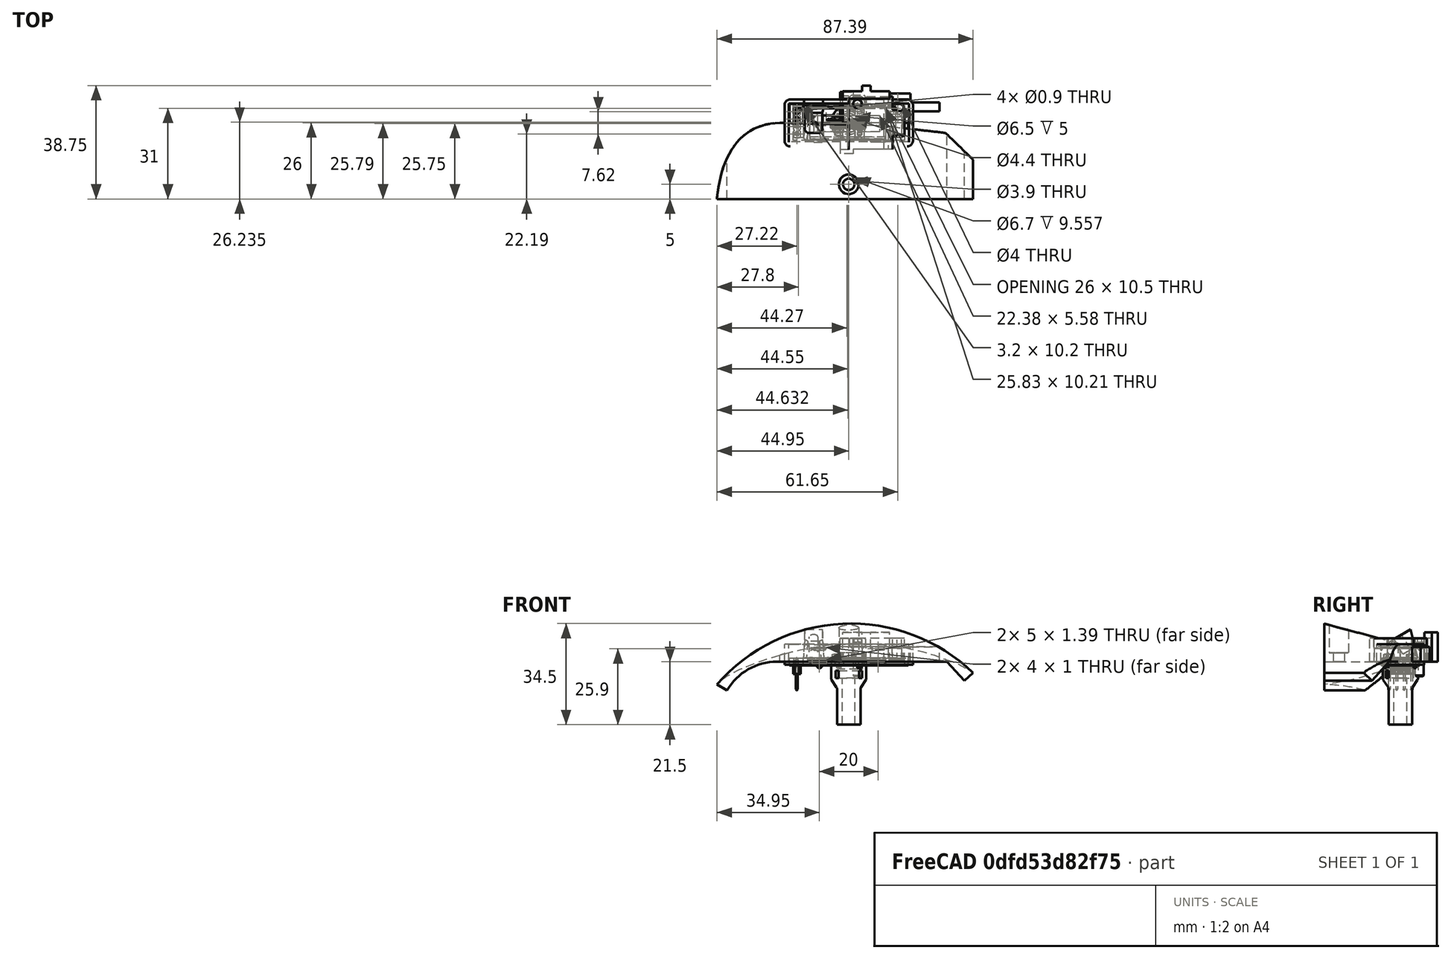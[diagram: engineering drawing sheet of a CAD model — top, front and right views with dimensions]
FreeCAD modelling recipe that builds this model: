
FCSTD DOCUMENT  (FreeCAD 1.0RUnknown)
Label: replicazeron
License: All rights reserved
LicenseURL: http://en.wikipedia.org/wiki/All_rights_reserved
objects: App::FeaturePython×45, Sketcher::SketchObject×26, Part::FeaturePython×17, PartDesign::CoordinateSystem×12, PartDesign::Pocket×10, PartDesign::Pad×8, App::Link×7, PartDesign::Body×7, App::DocumentObjectGroup×3, App::Part×3, PartDesign::Chamfer×3, PartDesign::Plane×2, PartDesign::Fillet×2, PartDesign::AdditiveLoft×2, PartDesign::Mirrored×2, Mesh::Feature×1, PartDesign::Revolution×1, PartDesign::SubtractiveLoft×1, PartDesign::PolarPattern×1, PartDesign::Hole×1
note: 180 computed .brp shape members not serialized (recipe doc carries the construction recipe); baked Part::Feature solids carry a one-line shape summary decoded from their .brp

FEATURE [PartDesign::CoordinateSystem] LCS_Origin
  AttacherType = Attacher::AttachEngine3D
  AttachmentSupport = -> [X_Axis]
  MapMode = 2
FEATURE [App::DocumentObjectGroup] Constraints
FEATURE [App::FeaturePython] Variables  # WARN: FeaturePython — macro-defined, semantics opaque (R4)
  Type = App::PropertyContainer
FEATURE [App::DocumentObjectGroup] Configurations
FEATURE [PartDesign::CoordinateSystem] LCS_0
  AttacherType = Attacher::AttachEngine3D
  AttachmentSupport = -> [X_Axis001]
  MapMode = 2
FEATURE [Sketcher::SketchObject] Sketch
  ArcFitTolerance = 0
  AttachmentSupport = -> [XY_Plane001]
  FullyConstrained = true
  MakeInternals = false
  MapMode = 5
  sketch-geometry (13):
    g0: LineSegment StartX=1.5 StartY=9 StartZ=0 EndX=15 EndY=9 EndZ=0
    g1: LineSegment StartX=15 StartY=-9 StartZ=0 EndX=1.5 EndY=-9 EndZ=0
    g2: LineSegment StartX=15 StartY=9 StartZ=0 EndX=15 EndY=4.5 EndZ=0
    g3: LineSegment StartX=15 StartY=4.5 StartZ=0 EndX=19 EndY=4.5 EndZ=0
    g4: LineSegment StartX=19 StartY=4.5 StartZ=0 EndX=19 EndY=-4.5 EndZ=0
    g5: LineSegment StartX=19 StartY=-4.5 StartZ=0 EndX=15 EndY=-4.5 EndZ=0
    g6: LineSegment StartX=15 StartY=-4.5 StartZ=0 EndX=15 EndY=-9 EndZ=0
    g7: LineSegment StartX=-3 StartY=10.5 StartZ=0 EndX=-3 EndY=-10.5 EndZ=0
    g8: LineSegment StartX=-3 StartY=10.5 StartZ=0 EndX=1.5 EndY=10.5 EndZ=0
    g9: LineSegment StartX=1.5 StartY=10.5 StartZ=0 EndX=1.5 EndY=9 EndZ=0
    g10: LineSegment StartX=1.5 StartY=-9 StartZ=0 EndX=1.5 EndY=-10.5 EndZ=0
    g11: LineSegment StartX=1.5 StartY=-10.5 StartZ=0 EndX=-3 EndY=-10.5 EndZ=0
    g12: LineSegment [constr] StartX=1.5 StartY=9 StartZ=0 EndX=1.5 EndY=-9 EndZ=0
  constraints (36):
    c: Horizontal(g0)
    c: Horizontal(g1)
    c: Symmetric(g0,g1,g-1)
    c: Coincident(g0,g2)
    c: Vertical(g2)
    c: Coincident(g2,g3)
    c: Horizontal(g3)
    c: Coincident(g3,g4)
    c: Coincident(g4,g5)
    c: Horizontal(g5)
    c: Coincident(g5,g6)
    c: Coincident(g6,g1)
    c: Vertical(g6)
    c: Symmetric(g4,g3,g-1)
    c: DistanceX(g3,g3) = 4
    c: DistanceY(g4,g4) = 9
    c: DistanceY(g1,g0) = 18
    c: Vertical(g7)
    c: Coincident(g7,g8)
    c: Horizontal(g8)
    c: Coincident(g8,g9)
    c: Coincident(g9,g0)
    c: Coincident(g1,g10)
    c: Coincident(g10,g11)
    c: Coincident(g11,g7)
    c: Horizontal(g11)
    c: Equal(g9,g10)
    c: DistanceY(g10,g10) = 1.5
    c: Vertical(g10)
    c: DistanceX(g3) = 19
    c: Vertical(g9)
    c: Coincident(g12,g0)
    c: Coincident(g12,g1)
    c: Vertical(g12)
    c: DistanceX(g7) = -3
    c: DistanceX(g0) = 1.5
FEATURE [PartDesign::Pad] Pad
  Direction = (0,0,1)
  Length = 8
  Length2 = 10
  Profile = -> Sketch
  ReferenceAxis = -> Sketch [N_Axis]
  Suppressed = false
  Type = 0
FEATURE [Sketcher::SketchObject] Sketch001
  ArcFitTolerance = 0
  AttachmentSupport = -> [XZ_Plane001]
  FullyConstrained = true
  MakeInternals = false
  MapMode = 5
  Placement = pos=(0,0,0) rot=(1,0,0;1.5708rad)
  sketch-geometry (4):
    g0: LineSegment StartX=-10 StartY=15 StartZ=0 EndX=0 EndY=15 EndZ=0
    g1: LineSegment StartX=0 StartY=15 StartZ=0 EndX=0 EndY=5 EndZ=0
    g2: LineSegment StartX=0 StartY=5 StartZ=0 EndX=-10 EndY=5 EndZ=0
    g3: LineSegment StartX=-10 StartY=5 StartZ=0 EndX=-10 EndY=15 EndZ=0
  constraints (12):
    c: Coincident(g0,g1)
    c: Coincident(g1,g2)
    c: Coincident(g2,g3)
    c: Coincident(g3,g0)
    c: Horizontal(g0)
    c: Horizontal(g2)
    c: Vertical(g1)
    c: Vertical(g3)
    c: PointOnObject(g0,g-2)
    c: DistanceY(g2) = 5
    c: Equal(g3,g2)
    c: DistanceX(g0,g0) = 10
FEATURE [PartDesign::Pocket] Pocket
  BaseFeature = -> Pad
  Direction = (0,1,-2e-16)
  Length = 18.2
  Length2 = 5
  Midplane = true
  Profile = -> Sketch001
  ReferenceAxis = -> Sketch001 [N_Axis]
  Suppressed = false
  Type = 0
FEATURE [Mesh::Feature] Thumb_spacer  label="Thumb spacer"
FEATURE [PartDesign::CoordinateSystem] LCS_0002
  AttacherType = Attacher::AttachEngine3D
  AttachmentSupport = -> [X_Axis003]
  MapMode = 2
FEATURE [Sketcher::SketchObject] Sketch005
  ArcFitTolerance = 0
  AttachmentSupport = -> [XY_Plane003]
  FullyConstrained = true
  MakeInternals = false
  MapMode = 5
  sketch-geometry (6):
    g0: LineSegment StartX=0 StartY=9.5 StartZ=0 EndX=6 EndY=9.5 EndZ=0
    g1: LineSegment StartX=6 StartY=9.5 StartZ=0 EndX=6 EndY=0 EndZ=0
    g2: LineSegment StartX=6 StartY=0 StartZ=0 EndX=0 EndY=0 EndZ=0
    g3: LineSegment StartX=0 StartY=0 StartZ=0 EndX=0 EndY=9.5 EndZ=0
    g4: Circle CenterX=3 CenterY=6.5 CenterZ=0 NormalX=0 NormalY=0 NormalZ=1 AngleXU=0 Radius=1.7
    g5: LineSegment [constr] StartX=0 StartY=6.5 StartZ=0 EndX=6 EndY=6.5 EndZ=0
  constraints (17):
    c: Coincident(g0,g1)
    c: Coincident(g1,g2)
    c: Coincident(g2,g3)
    c: Coincident(g3,g0)
    c: Horizontal(g0)
    c: Horizontal(g2)
    c: Vertical(g1)
    c: Vertical(g3)
    c: DistanceX(g0,g0) = 6
    c: DistanceY(g3,g3) = 9.5
    c: Coincident(g2,g-1)
    c: PointOnObject(g5,g3)
    c: PointOnObject(g5,g1)
    c: Horizontal(g5)
    c: Symmetric(g5,g5,g4)
    c: Diameter(g4) = 3.4
    c: DistanceY(g4) = 6.5
FEATURE [PartDesign::Pad] Pad002
  Direction = (0,0,1)
  Length = 5
  Length2 = 10
  Profile = -> Sketch005
  ReferenceAxis = -> Sketch005 [N_Axis]
  Suppressed = false
  Type = 0
FEATURE [PartDesign::CoordinateSystem] LCS_0003
  AttacherType = Attacher::AttachEngine3D
  AttachmentOffset = pos=(18.69,24.5,43) rot=(1,0,0;0.698132rad)
  AttachmentSupport = -> [X_Axis004]
  MapMode = 2
  Placement = pos=(18.69,24.5,43) rot=(1,0,0;0.698132rad)
FEATURE [App::Part] p_thumb_spacer
  Group = -> [LCS_0003,Thumb_spacer]
  Origin = -> Origin004
FEATURE [App::Link] thumb_spacer
  AssemblyType = Part::Link
  AttachedBy = #LCS_0003
  AttachedTo = Parent Assembly#LCS_Origin
  LinkPlacement = pos=(-18.69,-46.408,-17.1916) rot=(-1,0,0;0.698132rad)
  LinkedObject = -> p_thumb_spacer
  Placement = pos=(-18.69,-46.408,-17.1916) rot=(-1,0,0;0.698132rad)
  SolverId = Asm4EE
  expr: Placement = LCS_Origin.Placement * AttachmentOffset * LCS_0003.Placement ^ -1
FEATURE [App::Link] m3_attach
  AssemblyType = Part::Link
  AttachedBy = #LCS_0002
  AttachedTo = thumb_spacer#LCS_0003
  LinkPlacement = pos=(0,-7.1e-15,0) rot=(0,0,1;0rad)
  LinkedObject = -> b_m3_attach
  Placement = pos=(0,-7.1e-15,0) rot=(0,0,1;0rad)
  SolverId = Asm4EE
  expr: Placement = thumb_spacer.Placement * LCS_0003.Placement * AttachmentOffset * LCS_0002.Placement ^ -1
FEATURE [PartDesign::Chamfer] Chamfer
  Angle = 45
  Base = -> Pad002 [Edge2,Edge1]
  BaseFeature = -> Pad002
  ChamferType = 0
  FlipDirection = false
  Size = 1
  Size2 = 1
  SupportTransform = false
  Suppressed = false
  UseAllEdges = false
FEATURE [PartDesign::CoordinateSystem] LCS_1
  AttacherType = Attacher::AttachEngine3D
  AttachmentSupport = -> [Chamfer]
  MapMode = 11
  Placement = pos=(3,6.5,0) rot=(0,0,1;1.5708rad)
FEATURE [PartDesign::Body] b_m3_attach
  AllowCompound = false
  Group = -> [LCS_0002,Sketch005,Pad002,Chamfer,LCS_1]
  Origin = -> Origin003
  Tip = -> Chamfer
FEATURE [PartDesign::CoordinateSystem] LCS_0004
  AttacherType = Attacher::AttachEngine3D
  AttachmentSupport = -> [X_Axis005]
  MapMode = 2
FEATURE [Part::FeaturePython] b_Board_001_  label="Board_001"  # a2plus imported part (geometry in sourceFile) (typed FeaturePython)
  a2p_Version = V0.1
  fixedPosition = true
  objectType = a2pPart
  sourceFile = .\Board.FCStd
  subassemblyImport = false
  timeLastImport = 1.67313e+09
  updateColors = true
FEATURE [Part::FeaturePython] b_1x4_Male_Header_001_  label="1x4 Male Header_001"  # a2plus imported part (geometry in sourceFile) (typed FeaturePython)
  Placement = pos=(-17.73,3.81,-1.2) rot=(0.707107,-0.707107,0;3.14159rad)
  a2p_Version = V0.1
  fixedPosition = false
  objectType = a2pPart
  sourceFile = .\1x4 Male Header.FCStd
  subassemblyImport = false
  timeLastImport = 1.67313e+09
  updateColors = true
FEATURE [Part::FeaturePython] b_0603_Capacitor_001_  label="0603 Capacitor_001"  # a2plus imported part (geometry in sourceFile) (typed FeaturePython)
  Placement = pos=(-3.32202,-3.1568,-2.2) rot=(0,0,1;0rad)
  a2p_Version = V0.1
  fixedPosition = false
  objectType = a2pPart
  sourceFile = .\0603 Capacitor.FCStd
  subassemblyImport = false
  timeLastImport = 1.66767e+09
  updateColors = true
FEATURE [Part::FeaturePython] b_0603_Capacitor_001_001  label="0603 Capacitor_002"  # a2plus imported part (geometry in sourceFile) (typed FeaturePython)
  Placement = pos=(3.66323,-5.19401,-2.2) rot=(0,0,1;0rad)
  a2p_Version = V0.1
  fixedPosition = false
  objectType = a2pPart
  sourceFile = .\0603 Capacitor.FCStd
  subassemblyImport = false
  timeLastImport = 1.66767e+09
  updateColors = true
FEATURE [Part::FeaturePython] b_0603_Capacitor_001_002  label="0603 Capacitor_003"  # a2plus imported part (geometry in sourceFile) (typed FeaturePython)
  Placement = pos=(3.66323,-3.69266,-2.2) rot=(0,0,1;0rad)
  a2p_Version = V0.1
  fixedPosition = false
  objectType = a2pPart
  sourceFile = .\0603 Capacitor.FCStd
  subassemblyImport = false
  timeLastImport = 1.66767e+09
  updateColors = true
FEATURE [Part::FeaturePython] b_0603_Capacitor_001_003  label="0603 Capacitor_004"  # a2plus imported part (geometry in sourceFile) (typed FeaturePython)
  Placement = pos=(3.66323,-2.26045,-2.2) rot=(0,0,1;0rad)
  a2p_Version = V0.1
  fixedPosition = false
  objectType = a2pPart
  sourceFile = .\0603 Capacitor.FCStd
  subassemblyImport = false
  timeLastImport = 1.66767e+09
  updateColors = true
FEATURE [Part::FeaturePython] b_0603_Capacitor_001_004  label="0603 Capacitor_005"  # a2plus imported part (geometry in sourceFile) (typed FeaturePython)
  Placement = pos=(3.66324,-0.838123,-2.2) rot=(0,0,1;0rad)
  a2p_Version = V0.1
  fixedPosition = false
  objectType = a2pPart
  sourceFile = .\0603 Capacitor.FCStd
  subassemblyImport = false
  timeLastImport = 1.66767e+09
  updateColors = true
FEATURE [Part::FeaturePython] b_0603_Capacitor_001_005  label="0603 Capacitor_006"  # a2plus imported part (geometry in sourceFile) (typed FeaturePython)
  Placement = pos=(3.66324,2.11924,-2.2) rot=(0,0,1;0rad)
  a2p_Version = V0.1
  fixedPosition = false
  objectType = a2pPart
  sourceFile = .\0603 Capacitor.FCStd
  subassemblyImport = false
  timeLastImport = 1.66767e+09
  updateColors = true
FEATURE [Part::FeaturePython] b_0603_Capacitor_001_006  label="0603 Capacitor_007"  # a2plus imported part (geometry in sourceFile) (typed FeaturePython)
  Placement = pos=(3.66325,3.579,-2.2) rot=(0,0,1;0rad)
  a2p_Version = V0.1
  fixedPosition = false
  objectType = a2pPart
  sourceFile = .\0603 Capacitor.FCStd
  subassemblyImport = false
  timeLastImport = 1.66767e+09
  updateColors = true
FEATURE [Part::FeaturePython] b_0603_Capacitor_001_007  label="0603 Capacitor_008"  # a2plus imported part (geometry in sourceFile) (typed FeaturePython)
  Placement = pos=(3.66325,4.96638,-2.2) rot=(0,0,1;0rad)
  a2p_Version = V0.1
  fixedPosition = false
  objectType = a2pPart
  sourceFile = .\0603 Capacitor.FCStd
  subassemblyImport = false
  timeLastImport = 1.66767e+09
  updateColors = true
FEATURE [Part::FeaturePython] b_0603_Resistor_001_  label="0603 Resistor_001"  # a2plus imported part (geometry in sourceFile) (typed FeaturePython)
  Placement = pos=(-3.32202,-0.277574,-1.7) rot=(0,0,1;0rad)
  a2p_Version = V0.1
  fixedPosition = false
  objectType = a2pPart
  sourceFile = .\0603 Resistor.FCStd
  subassemblyImport = false
  timeLastImport = 1.66767e+09
  updateColors = true
FEATURE [App::FeaturePython] planeCoincident_003  label="planeCoincident_003__0603 Capacitor_002"  # a2plus constraint (typed FeaturePython)
  Object1 = b_0603_Capacitor_001_
  Object2 = b_0603_Capacitor_001_001
  ParentTreeObject = -> b_0603_Capacitor_001_
  SubElement1 = Face11
  SubElement2 = Face11
  Suppressed = false
  Type = plane
  directionConstraint = 0
  offset = 0
FEATURE [App::FeaturePython] planeCoincident_003_mirror  label="planeCoincident_003__0603 Capacitor_001"  # a2plus constraint (typed FeaturePython)
  Object1 = b_0603_Capacitor_001_
  Object2 = b_0603_Capacitor_001_001
  ParentTreeObject = -> b_0603_Capacitor_001_001
  SubElement1 = Face11
  SubElement2 = Face11
  Suppressed = false
  Type = plane
  directionConstraint = 0
  offset = 0
FEATURE [App::FeaturePython] planeCoincident_004  label="planeCoincident_004__0603 Capacitor_002"  # a2plus constraint (typed FeaturePython)
  Object1 = b_0603_Capacitor_001_002
  Object2 = b_0603_Capacitor_001_001
  ParentTreeObject = -> b_0603_Capacitor_001_002
  SubElement1 = Face11
  SubElement2 = Face11
  Suppressed = false
  Type = plane
  directionConstraint = 0
  offset = 0
FEATURE [App::FeaturePython] planeCoincident_004_mirror  label="planeCoincident_004__0603 Capacitor_003"  # a2plus constraint (typed FeaturePython)
  Object1 = b_0603_Capacitor_001_002
  Object2 = b_0603_Capacitor_001_001
  ParentTreeObject = -> b_0603_Capacitor_001_001
  SubElement1 = Face11
  SubElement2 = Face11
  Suppressed = false
  Type = plane
  directionConstraint = 0
  offset = 0
FEATURE [App::FeaturePython] planeCoincident_005  label="planeCoincident_005__0603 Capacitor_003"  # a2plus constraint (typed FeaturePython)
  Object1 = b_0603_Capacitor_001_003
  Object2 = b_0603_Capacitor_001_002
  ParentTreeObject = -> b_0603_Capacitor_001_003
  SubElement1 = Face11
  SubElement2 = Face11
  Suppressed = false
  Type = plane
  directionConstraint = 0
  offset = 0
FEATURE [App::FeaturePython] planeCoincident_005_mirror  label="planeCoincident_005__0603 Capacitor_004"  # a2plus constraint (typed FeaturePython)
  Object1 = b_0603_Capacitor_001_003
  Object2 = b_0603_Capacitor_001_002
  ParentTreeObject = -> b_0603_Capacitor_001_002
  SubElement1 = Face11
  SubElement2 = Face11
  Suppressed = false
  Type = plane
  directionConstraint = 0
  offset = 0
FEATURE [App::FeaturePython] planeCoincident_006  label="planeCoincident_006__0603 Capacitor_004"  # a2plus constraint (typed FeaturePython)
  Object1 = b_0603_Capacitor_001_004
  Object2 = b_0603_Capacitor_001_003
  ParentTreeObject = -> b_0603_Capacitor_001_004
  SubElement1 = Face11
  SubElement2 = Face11
  Suppressed = false
  Type = plane
  directionConstraint = 0
  offset = 0
FEATURE [App::FeaturePython] planeCoincident_006_mirror  label="planeCoincident_006__0603 Capacitor_005"  # a2plus constraint (typed FeaturePython)
  Object1 = b_0603_Capacitor_001_004
  Object2 = b_0603_Capacitor_001_003
  ParentTreeObject = -> b_0603_Capacitor_001_003
  SubElement1 = Face11
  SubElement2 = Face11
  Suppressed = false
  Type = plane
  directionConstraint = 0
  offset = 0
FEATURE [App::FeaturePython] planeCoincident_007  label="planeCoincident_007__0603 Capacitor_005"  # a2plus constraint (typed FeaturePython)
  Object1 = b_0603_Capacitor_001_005
  Object2 = b_0603_Capacitor_001_004
  ParentTreeObject = -> b_0603_Capacitor_001_005
  SubElement1 = Face11
  SubElement2 = Face11
  Suppressed = false
  Type = plane
  directionConstraint = 0
  offset = 0
FEATURE [App::FeaturePython] planeCoincident_007_mirror  label="planeCoincident_007__0603 Capacitor_006"  # a2plus constraint (typed FeaturePython)
  Object1 = b_0603_Capacitor_001_005
  Object2 = b_0603_Capacitor_001_004
  ParentTreeObject = -> b_0603_Capacitor_001_004
  SubElement1 = Face11
  SubElement2 = Face11
  Suppressed = false
  Type = plane
  directionConstraint = 0
  offset = 0
FEATURE [App::FeaturePython] planeCoincident_008  label="planeCoincident_008__0603 Capacitor_006"  # a2plus constraint (typed FeaturePython)
  Object1 = b_0603_Capacitor_001_006
  Object2 = b_0603_Capacitor_001_005
  ParentTreeObject = -> b_0603_Capacitor_001_006
  SubElement1 = Face11
  SubElement2 = Face11
  Suppressed = false
  Type = plane
  directionConstraint = 0
  offset = 0
FEATURE [App::FeaturePython] planeCoincident_008_mirror  label="planeCoincident_008__0603 Capacitor_007"  # a2plus constraint (typed FeaturePython)
  Object1 = b_0603_Capacitor_001_006
  Object2 = b_0603_Capacitor_001_005
  ParentTreeObject = -> b_0603_Capacitor_001_005
  SubElement1 = Face11
  SubElement2 = Face11
  Suppressed = false
  Type = plane
  directionConstraint = 0
  offset = 0
FEATURE [App::FeaturePython] planeCoincident_009  label="planeCoincident_009__0603 Capacitor_007"  # a2plus constraint (typed FeaturePython)
  Object1 = b_0603_Capacitor_001_007
  Object2 = b_0603_Capacitor_001_006
  ParentTreeObject = -> b_0603_Capacitor_001_007
  SubElement1 = Face11
  SubElement2 = Face11
  Suppressed = false
  Type = plane
  directionConstraint = 0
  offset = 0
FEATURE [App::FeaturePython] planeCoincident_009_mirror  label="planeCoincident_009__0603 Capacitor_008"  # a2plus constraint (typed FeaturePython)
  Object1 = b_0603_Capacitor_001_007
  Object2 = b_0603_Capacitor_001_006
  ParentTreeObject = -> b_0603_Capacitor_001_006
  SubElement1 = Face11
  SubElement2 = Face11
  Suppressed = false
  Type = plane
  directionConstraint = 0
  offset = 0
FEATURE [App::FeaturePython] planeCoincident_010  label="planeCoincident_010__0603 Capacitor_003"  # a2plus constraint (typed FeaturePython)
  Object1 = b_0603_Capacitor_001_001
  Object2 = b_0603_Capacitor_001_002
  ParentTreeObject = -> b_0603_Capacitor_001_001
  SubElement1 = Face14
  SubElement2 = Face14
  Suppressed = false
  Type = plane
  directionConstraint = 0
  offset = 0
FEATURE [App::FeaturePython] planeCoincident_010_mirror  label="planeCoincident_010__0603 Capacitor_002"  # a2plus constraint (typed FeaturePython)
  Object1 = b_0603_Capacitor_001_001
  Object2 = b_0603_Capacitor_001_002
  ParentTreeObject = -> b_0603_Capacitor_001_002
  SubElement1 = Face14
  SubElement2 = Face14
  Suppressed = false
  Type = plane
  directionConstraint = 0
  offset = 0
FEATURE [App::FeaturePython] planeCoincident_011  label="planeCoincident_011__0603 Capacitor_004"  # a2plus constraint (typed FeaturePython)
  Object1 = b_0603_Capacitor_001_002
  Object2 = b_0603_Capacitor_001_003
  ParentTreeObject = -> b_0603_Capacitor_001_002
  SubElement1 = Face14
  SubElement2 = Face14
  Suppressed = false
  Type = plane
  directionConstraint = 0
  offset = 0
FEATURE [App::FeaturePython] planeCoincident_011_mirror  label="planeCoincident_011__0603 Capacitor_003"  # a2plus constraint (typed FeaturePython)
  Object1 = b_0603_Capacitor_001_002
  Object2 = b_0603_Capacitor_001_003
  ParentTreeObject = -> b_0603_Capacitor_001_003
  SubElement1 = Face14
  SubElement2 = Face14
  Suppressed = false
  Type = plane
  directionConstraint = 0
  offset = 0
FEATURE [App::FeaturePython] planeCoincident_012  label="planeCoincident_012__0603 Capacitor_005"  # a2plus constraint (typed FeaturePython)
  Object1 = b_0603_Capacitor_001_003
  Object2 = b_0603_Capacitor_001_004
  ParentTreeObject = -> b_0603_Capacitor_001_003
  SubElement1 = Face14
  SubElement2 = Face14
  Suppressed = false
  Type = plane
  directionConstraint = 0
  offset = 0
FEATURE [App::FeaturePython] planeCoincident_012_mirror  label="planeCoincident_012__0603 Capacitor_004"  # a2plus constraint (typed FeaturePython)
  Object1 = b_0603_Capacitor_001_003
  Object2 = b_0603_Capacitor_001_004
  ParentTreeObject = -> b_0603_Capacitor_001_004
  SubElement1 = Face14
  SubElement2 = Face14
  Suppressed = false
  Type = plane
  directionConstraint = 0
  offset = 0
FEATURE [App::FeaturePython] planeCoincident_013  label="planeCoincident_013__0603 Capacitor_006"  # a2plus constraint (typed FeaturePython)
  Object1 = b_0603_Capacitor_001_004
  Object2 = b_0603_Capacitor_001_005
  ParentTreeObject = -> b_0603_Capacitor_001_004
  SubElement1 = Face14
  SubElement2 = Face14
  Suppressed = false
  Type = plane
  directionConstraint = 0
  offset = 0
FEATURE [App::FeaturePython] planeCoincident_013_mirror  label="planeCoincident_013__0603 Capacitor_005"  # a2plus constraint (typed FeaturePython)
  Object1 = b_0603_Capacitor_001_004
  Object2 = b_0603_Capacitor_001_005
  ParentTreeObject = -> b_0603_Capacitor_001_005
  SubElement1 = Face14
  SubElement2 = Face14
  Suppressed = false
  Type = plane
  directionConstraint = 0
  offset = 0
FEATURE [App::FeaturePython] planeCoincident_014  label="planeCoincident_014__0603 Capacitor_005"  # a2plus constraint (typed FeaturePython)
  Object1 = b_0603_Capacitor_001_005
  Object2 = b_0603_Capacitor_001_004
  ParentTreeObject = -> b_0603_Capacitor_001_005
  SubElement1 = Face14
  SubElement2 = Face14
  Suppressed = false
  Type = plane
  directionConstraint = 0
  offset = 0
FEATURE [App::FeaturePython] planeCoincident_014_mirror  label="planeCoincident_014__0603 Capacitor_006"  # a2plus constraint (typed FeaturePython)
  Object1 = b_0603_Capacitor_001_005
  Object2 = b_0603_Capacitor_001_004
  ParentTreeObject = -> b_0603_Capacitor_001_004
  SubElement1 = Face14
  SubElement2 = Face14
  Suppressed = false
  Type = plane
  directionConstraint = 0
  offset = 0
FEATURE [App::FeaturePython] planeCoincident_015  label="planeCoincident_015__0603 Capacitor_006"  # a2plus constraint (typed FeaturePython)
  Object1 = b_0603_Capacitor_001_006
  Object2 = b_0603_Capacitor_001_005
  ParentTreeObject = -> b_0603_Capacitor_001_006
  SubElement1 = Face14
  SubElement2 = Face14
  Suppressed = false
  Type = plane
  directionConstraint = 0
  offset = 0
FEATURE [App::FeaturePython] planeCoincident_015_mirror  label="planeCoincident_015__0603 Capacitor_007"  # a2plus constraint (typed FeaturePython)
  Object1 = b_0603_Capacitor_001_006
  Object2 = b_0603_Capacitor_001_005
  ParentTreeObject = -> b_0603_Capacitor_001_005
  SubElement1 = Face14
  SubElement2 = Face14
  Suppressed = false
  Type = plane
  directionConstraint = 0
  offset = 0
FEATURE [App::FeaturePython] planeCoincident_016  label="planeCoincident_016__0603 Capacitor_008"  # a2plus constraint (typed FeaturePython)
  Object1 = b_0603_Capacitor_001_006
  Object2 = b_0603_Capacitor_001_007
  ParentTreeObject = -> b_0603_Capacitor_001_006
  SubElement1 = Face14
  SubElement2 = Face14
  Suppressed = false
  Type = plane
  directionConstraint = 0
  offset = 0
FEATURE [App::FeaturePython] planeCoincident_016_mirror  label="planeCoincident_016__0603 Capacitor_007"  # a2plus constraint (typed FeaturePython)
  Object1 = b_0603_Capacitor_001_006
  Object2 = b_0603_Capacitor_001_007
  ParentTreeObject = -> b_0603_Capacitor_001_007
  SubElement1 = Face14
  SubElement2 = Face14
  Suppressed = false
  Type = plane
  directionConstraint = 0
  offset = 0
FEATURE [Part::FeaturePython] b_0603_Resistor_001_001  label="0603 Resistor_002"  # a2plus imported part (geometry in sourceFile) (typed FeaturePython)
  Placement = pos=(-3.32202,1.20536,-1.7) rot=(0,0,1;0rad)
  a2p_Version = V0.1
  fixedPosition = false
  objectType = a2pPart
  sourceFile = .\0603 Resistor.FCStd
  subassemblyImport = false
  timeLastImport = 1.66767e+09
  updateColors = true
FEATURE [Part::FeaturePython] b_0603_Resistor_001_002  label="0603 Resistor_003"  # a2plus imported part (geometry in sourceFile) (typed FeaturePython)
  Placement = pos=(-3.32202,2.82623,-1.7) rot=(0,0,1;0rad)
  a2p_Version = V0.1
  fixedPosition = false
  objectType = a2pPart
  sourceFile = .\0603 Resistor.FCStd
  subassemblyImport = false
  timeLastImport = 1.66767e+09
  updateColors = true
FEATURE [Part::FeaturePython] b_0603_Resistor_001_003  label="0603 Resistor_004"  # a2plus imported part (geometry in sourceFile) (typed FeaturePython)
  Placement = pos=(3.66325,0.630687,-1.7) rot=(0,0,1;0rad)
  a2p_Version = V0.1
  fixedPosition = false
  objectType = a2pPart
  sourceFile = .\0603 Resistor.FCStd
  subassemblyImport = false
  timeLastImport = 1.66767e+09
  updateColors = true
FEATURE [App::FeaturePython] planeCoincident_017  label="planeCoincident_017__0603 Resistor_002"  # a2plus constraint (typed FeaturePython)
  Object1 = b_0603_Resistor_001_
  Object2 = b_0603_Resistor_001_001
  ParentTreeObject = -> b_0603_Resistor_001_
  SubElement1 = Face11
  SubElement2 = Face11
  Suppressed = false
  Type = plane
  directionConstraint = 0
  offset = 0
FEATURE [App::FeaturePython] planeCoincident_017_mirror  label="planeCoincident_017__0603 Resistor_001"  # a2plus constraint (typed FeaturePython)
  Object1 = b_0603_Resistor_001_
  Object2 = b_0603_Resistor_001_001
  ParentTreeObject = -> b_0603_Resistor_001_001
  SubElement1 = Face11
  SubElement2 = Face11
  Suppressed = false
  Type = plane
  directionConstraint = 0
  offset = 0
FEATURE [App::FeaturePython] planeCoincident_018  label="planeCoincident_018__0603 Resistor_003"  # a2plus constraint (typed FeaturePython)
  Object1 = b_0603_Resistor_001_001
  Object2 = b_0603_Resistor_001_002
  ParentTreeObject = -> b_0603_Resistor_001_001
  SubElement1 = Face11
  SubElement2 = Face11
  Suppressed = false
  Type = plane
  directionConstraint = 0
  offset = 0
FEATURE [App::FeaturePython] planeCoincident_018_mirror  label="planeCoincident_018__0603 Resistor_002"  # a2plus constraint (typed FeaturePython)
  Object1 = b_0603_Resistor_001_001
  Object2 = b_0603_Resistor_001_002
  ParentTreeObject = -> b_0603_Resistor_001_002
  SubElement1 = Face11
  SubElement2 = Face11
  Suppressed = false
  Type = plane
  directionConstraint = 0
  offset = 0
FEATURE [App::FeaturePython] planeCoincident_019  label="planeCoincident_019__0603 Resistor_004"  # a2plus constraint (typed FeaturePython)
  Object1 = b_0603_Resistor_001_002
  Object2 = b_0603_Resistor_001_003
  ParentTreeObject = -> b_0603_Resistor_001_002
  SubElement1 = Face11
  SubElement2 = Face11
  Suppressed = false
  Type = plane
  directionConstraint = 0
  offset = 0
FEATURE [App::FeaturePython] planeCoincident_019_mirror  label="planeCoincident_019__0603 Resistor_003"  # a2plus constraint (typed FeaturePython)
  Object1 = b_0603_Resistor_001_002
  Object2 = b_0603_Resistor_001_003
  ParentTreeObject = -> b_0603_Resistor_001_003
  SubElement1 = Face11
  SubElement2 = Face11
  Suppressed = false
  Type = plane
  directionConstraint = 0
  offset = 0
FEATURE [App::FeaturePython] planeCoincident_020  label="planeCoincident_020__0603 Resistor_001"  # a2plus constraint (typed FeaturePython)
  Object1 = b_0603_Capacitor_001_
  Object2 = b_0603_Resistor_001_
  ParentTreeObject = -> b_0603_Capacitor_001_
  SubElement1 = Face14
  SubElement2 = Face14
  Suppressed = false
  Type = plane
  directionConstraint = 0
  offset = 0
FEATURE [App::FeaturePython] planeCoincident_020_mirror  label="planeCoincident_020__0603 Capacitor_001"  # a2plus constraint (typed FeaturePython)
  Object1 = b_0603_Capacitor_001_
  Object2 = b_0603_Resistor_001_
  ParentTreeObject = -> b_0603_Resistor_001_
  SubElement1 = Face14
  SubElement2 = Face14
  Suppressed = false
  Type = plane
  directionConstraint = 0
  offset = 0
FEATURE [App::FeaturePython] planeCoincident_021  label="planeCoincident_021__0603 Resistor_002"  # a2plus constraint (typed FeaturePython)
  Object1 = b_0603_Resistor_001_
  Object2 = b_0603_Resistor_001_001
  ParentTreeObject = -> b_0603_Resistor_001_
  SubElement1 = Face14
  SubElement2 = Face14
  Suppressed = false
  Type = plane
  directionConstraint = 0
  offset = 0
FEATURE [App::FeaturePython] planeCoincident_021_mirror  label="planeCoincident_021__0603 Resistor_001"  # a2plus constraint (typed FeaturePython)
  Object1 = b_0603_Resistor_001_
  Object2 = b_0603_Resistor_001_001
  ParentTreeObject = -> b_0603_Resistor_001_001
  SubElement1 = Face14
  SubElement2 = Face14
  Suppressed = false
  Type = plane
  directionConstraint = 0
  offset = 0
FEATURE [App::FeaturePython] planeCoincident_022  label="planeCoincident_022__0603 Resistor_003"  # a2plus constraint (typed FeaturePython)
  Object1 = b_0603_Resistor_001_001
  Object2 = b_0603_Resistor_001_002
  ParentTreeObject = -> b_0603_Resistor_001_001
  SubElement1 = Face14
  SubElement2 = Face14
  Suppressed = false
  Type = plane
  directionConstraint = 0
  offset = 0
FEATURE [App::FeaturePython] planeCoincident_022_mirror  label="planeCoincident_022__0603 Resistor_002"  # a2plus constraint (typed FeaturePython)
  Object1 = b_0603_Resistor_001_001
  Object2 = b_0603_Resistor_001_002
  ParentTreeObject = -> b_0603_Resistor_001_002
  SubElement1 = Face14
  SubElement2 = Face14
  Suppressed = false
  Type = plane
  directionConstraint = 0
  offset = 0
FEATURE [App::FeaturePython] planeCoincident_023  label="planeCoincident_023__0603 Capacitor_006"  # a2plus constraint (typed FeaturePython)
  Object1 = b_0603_Resistor_001_003
  Object2 = b_0603_Capacitor_001_005
  ParentTreeObject = -> b_0603_Resistor_001_003
  SubElement1 = Face14
  SubElement2 = Face14
  Suppressed = false
  Type = plane
  directionConstraint = 0
  offset = 0
FEATURE [App::FeaturePython] planeCoincident_023_mirror  label="planeCoincident_023__0603 Resistor_004"  # a2plus constraint (typed FeaturePython)
  Object1 = b_0603_Resistor_001_003
  Object2 = b_0603_Capacitor_001_005
  ParentTreeObject = -> b_0603_Capacitor_001_005
  SubElement1 = Face14
  SubElement2 = Face14
  Suppressed = false
  Type = plane
  directionConstraint = 0
  offset = 0
FEATURE [Part::FeaturePython] b_0603_Resistor_001_004  label="0603 Resistor_005"  # a2plus imported part (geometry in sourceFile) (typed FeaturePython)
  Placement = pos=(-3.33805,-1.73146,-1.7) rot=(0,0,1;0rad)
  a2p_Version = V0.1
  fixedPosition = false
  objectType = a2pPart
  sourceFile = .\0603 Resistor.FCStd
  subassemblyImport = false
  timeLastImport = 1.66767e+09
  updateColors = true
FEATURE [App::FeaturePython] planeCoincident_024  label="planeCoincident_024__0603 Resistor_005"  # a2plus constraint (typed FeaturePython)
  Object1 = b_0603_Resistor_001_
  Object2 = b_0603_Resistor_001_004
  ParentTreeObject = -> b_0603_Resistor_001_
  SubElement1 = Face11
  SubElement2 = Face11
  Suppressed = false
  Type = plane
  directionConstraint = 0
  offset = 0
FEATURE [App::FeaturePython] planeCoincident_024_mirror  label="planeCoincident_024__0603 Resistor_001"  # a2plus constraint (typed FeaturePython)
  Object1 = b_0603_Resistor_001_
  Object2 = b_0603_Resistor_001_004
  ParentTreeObject = -> b_0603_Resistor_001_004
  SubElement1 = Face11
  SubElement2 = Face11
  Suppressed = false
  Type = plane
  directionConstraint = 0
  offset = 0
FEATURE [Part::FeaturePython] b_Surface_Mount_Transistor_001_  label="Surface Mount Transistor_001"  # a2plus imported part (geometry in sourceFile) (typed FeaturePython)
  Placement = pos=(-9.99828,-1.25881,-1.2) rot=(0.707107,-0.707107,0;3.14159rad)
  a2p_Version = V0.1
  fixedPosition = false
  objectType = a2pPart
  sourceFile = .\Surface Mount Transistor.FCStd
  subassemblyImport = false
  timeLastImport = 1.65098e+09
  updateColors = true
FEATURE [App::Part] p_oled
  Group = -> [LCS_0004,b_Board_001_,b_1x4_Male_Header_001_,planeCoincident_020,planeCoincident_003,b_0603_Capacitor_001_,planeCoincident_004,planeCoincident_005_mirror,planeCoincident_010_mirror,planeCoincident_011,b_0603_Capacitor_001_002,planeCoincident_005,planeCoincident_006_mirror,planeCoincident_011_mirror,planeCoincident_012,b_0603_Capacitor_001_003,planeCoincident_006,planeCoincident_007_mirror,+43 more]
  Origin = -> Origin005
FEATURE [App::Link] oled
  AssemblyType = Part::Link
  AttachedBy = #LCS_0004
  AttachedTo = oled_case_bottom#LCS_2
  AttachmentOffset = pos=(0.5,0,-2.7) rot=(1,0,0;3.14159rad)
  LinkPlacement = pos=(-9.5,11.35,-10.1325) rot=(0,0.965926,0.258819;3.14159rad)
  LinkedObject = -> p_oled
  Placement = pos=(-9.5,11.35,-10.1325) rot=(0,0.965926,0.258819;3.14159rad)
  SolverId = Asm4EE
  expr: Placement = oled_case_bottom.Placement * LCS_2.Placement * AttachmentOffset * LCS_0004.Placement ^ -1
FEATURE [App::Link] oled_case_bottom
  AssemblyType = Part::Link
  AttachedBy = #LCS_2
  AttachedTo = m3_attach#LCS_1
  AttachmentOffset = pos=(0,0,0) rot=(0,0,1;1.5708rad)
  LinkPlacement = pos=(-9,10,-7.79423) rot=(0,-0.258819,0.965926;3.14159rad)
  LinkedObject = -> b_oled_case_bottom
  Placement = pos=(-9,10,-7.79423) rot=(0,-0.258819,0.965926;3.14159rad)
  SolverId = Asm4EE
  expr: Placement = m3_attach.Placement * LCS_1.Placement * AttachmentOffset * LCS_0005.Placement ^ -1
FEATURE [PartDesign::CoordinateSystem] LCS_2
  AttacherType = Attacher::AttachEngine3D
  AttachmentSupport = -> [X_Axis006]
  MapMode = 2
FEATURE [PartDesign::Plane] DatumPlane
  AttachmentSupport = -> [LCS_2]
  Length = 60
  MapMode = 5
  ResizeMode = 0
  Width = 60
FEATURE [Sketcher::SketchObject] Sketch007
  ArcFitTolerance = 0
  AttachmentSupport = -> [DatumPlane]
  FullyConstrained = true
  MakeInternals = false
  MapMode = 5
  sketch-geometry (8):
    g0: LineSegment StartX=-18.75 StartY=5.1 StartZ=0 EndX=-15.55 EndY=5.1 EndZ=0
    g1: LineSegment StartX=-15.55 StartY=5.1 StartZ=0 EndX=-15.55 EndY=-5.1 EndZ=0
    g2: LineSegment StartX=-15.55 StartY=-5.1 StartZ=0 EndX=-18.75 EndY=-5.1 EndZ=0
    g3: LineSegment StartX=-18.75 StartY=-5.1 StartZ=0 EndX=-18.75 EndY=5.1 EndZ=0
    g4: LineSegment StartX=-20.25 StartY=6.5 StartZ=0 EndX=20.25 EndY=6.5 EndZ=0
    g5: LineSegment StartX=20.25 StartY=6.5 StartZ=0 EndX=20.25 EndY=-6.5 EndZ=0
    g6: LineSegment StartX=20.25 StartY=-6.5 StartZ=0 EndX=-20.25 EndY=-6.5 EndZ=0
    g7: LineSegment StartX=-20.25 StartY=-6.5 StartZ=0 EndX=-20.25 EndY=6.5 EndZ=0
  constraints (21):
    c: Coincident(g0,g1)
    c: Coincident(g1,g2)
    c: Coincident(g2,g3)
    c: Coincident(g3,g0)
    c: Horizontal(g0)
    c: Horizontal(g2)
    c: Vertical(g3)
    c: Coincident(g4,g5)
    c: Coincident(g5,g6)
    c: Coincident(g6,g7)
    c: Coincident(g7,g4)
    c: Horizontal(g6)
    c: Vertical(g7)
    c: DistanceX(g4,g4) = 40.5
    c: DistanceX(g4,g0) = 1.5
    c: DistanceY(g3,g3) = 10.2
    c: DistanceX(g0,g0) = 3.2
    c: DistanceY(g5,g5) = 13
    c: Symmetric(g4,g4,g-2)
    c: Symmetric(g4,g5,g-1)
    c: Symmetric(g0,g1,g-1)
FEATURE [PartDesign::Pad] Pad003
  Direction = (0,0,1)
  Length = 2.5
  Length2 = 10
  Midplane = true
  Profile = -> Sketch007
  ReferenceAxis = -> Sketch007 [N_Axis]
  Reversed = true
  Suppressed = false
  Type = 0
FEATURE [Sketcher::SketchObject] Sketch008
  ArcFitTolerance = 0
  AttachmentOffset = pos=(-12,0,1) rot=(0,0,1;0rad)
  AttachmentSupport = -> [DatumPlane]
  FullyConstrained = true
  MakeInternals = false
  MapMode = 5
  Placement = pos=(-12,0,1) rot=(0,0,1;0rad)
  sketch-geometry (4):
    g0: LineSegment StartX=-3.5 StartY=-6 StartZ=0 EndX=3.5 EndY=-6 EndZ=0
    g1: LineSegment StartX=3.5 StartY=-6 StartZ=0 EndX=3.5 EndY=6 EndZ=0
    g2: LineSegment StartX=3.5 StartY=6 StartZ=0 EndX=-3.5 EndY=6 EndZ=0
    g3: LineSegment StartX=-3.5 StartY=6 StartZ=0 EndX=-3.5 EndY=-6 EndZ=0
  constraints (10):
    c: Coincident(g0,g1)
    c: Coincident(g1,g2)
    c: Coincident(g2,g3)
    c: Coincident(g3,g0)
    c: Horizontal(g0)
    c: Vertical(g3)
    c: DistanceX(g0,g0) = 7
    c: DistanceY(g3,g3) = 12
    c: Symmetric(g1,g0,g-1)
    c: Symmetric(g1,g2,g-2)
FEATURE [PartDesign::CoordinateSystem] LCS_0006
  AttacherType = Attacher::AttachEngine3D
  AttachmentSupport = -> [X_Axis007]
  MapMode = 2
FEATURE [Sketcher::SketchObject] Sketch010
  ArcFitTolerance = 0
  AttachmentSupport = -> [XY_Plane007]
  FullyConstrained = true
  MakeInternals = false
  MapMode = 5
  sketch-geometry (8):
    g0: LineSegment StartX=-21.9 StartY=8.025 StartZ=0 EndX=21.9 EndY=8.025 EndZ=0
    g1: LineSegment StartX=21.9 StartY=8.025 StartZ=0 EndX=21.9 EndY=-8.025 EndZ=0
    g2: LineSegment StartX=21.9 StartY=-8.025 StartZ=0 EndX=-21.9 EndY=-8.025 EndZ=0
    g3: LineSegment StartX=-21.9 StartY=-8.025 StartZ=0 EndX=-21.9 EndY=8.025 EndZ=0
    g4: LineSegment StartX=-20.5 StartY=6.625 StartZ=0 EndX=20.5 EndY=6.625 EndZ=0
    g5: LineSegment StartX=20.5 StartY=6.625 StartZ=0 EndX=20.5 EndY=-6.625 EndZ=0
    g6: LineSegment StartX=20.5 StartY=-6.625 StartZ=0 EndX=-20.5 EndY=-6.625 EndZ=0
    g7: LineSegment StartX=-20.5 StartY=-6.625 StartZ=0 EndX=-20.5 EndY=6.625 EndZ=0
  constraints (21):
    c: Coincident(g0,g1)
    c: Coincident(g1,g2)
    c: Coincident(g2,g3)
    c: Coincident(g3,g0)
    c: Horizontal(g2)
    c: Vertical(g1)
    c: Symmetric(g0,g0,g-2)
    c: Coincident(g4,g5)
    c: Coincident(g5,g6)
    c: Coincident(g6,g7)
    c: Coincident(g7,g4)
    c: Horizontal(g6)
    c: Vertical(g5)
    c: Symmetric(g4,g4,g-2)
    c: DistanceX(g0,g4) = 1.4
    c: DistanceY(g4,g0) = 1.4
    c: DistanceY(g2,g6) = 1.4
    c: Vertical(g3)
    c: DistanceX(g4,g4) = 41
    c: DistanceY(g7,g7) = 13.25
    c: Symmetric(g4,g6,g-1)
FEATURE [App::Link] oled_case_top
  AssemblyType = Part::Link
  AttachedBy = #LCS_0006
  AttachedTo = oled_case_bottom#LCS_2
  AttachmentOffset = pos=(0,0,-4.4) rot=(0,0,1;0rad)
  LinkPlacement = pos=(-9,12.2,-11.6047) rot=(0,-0.258819,0.965926;3.14159rad)
  LinkedObject = -> b_oled_case_top
  Placement = pos=(-9,12.2,-11.6047) rot=(0,-0.258819,0.965926;3.14159rad)
  SolverId = Asm4EE
  expr: Placement = oled_case_bottom.Placement * LCS_2.Placement * AttachmentOffset * LCS_0006.Placement ^ -1
FEATURE [PartDesign::Pad] Pad004
  Direction = (0,0,1)
  Length = 6
  Length2 = 10
  Profile = -> Sketch010
  ReferenceAxis = -> Sketch010 [N_Axis]
  Suppressed = false
  Type = 0
FEATURE [Sketcher::SketchObject] Sketch011
  ArcFitTolerance = 0
  AttachmentSupport = -> [XY_Plane007]
  ExternalGeometry = -> [Pad004]
  FullyConstrained = false
  MakeInternals = false
  MapMode = 5
  sketch-geometry (8):
    g0: LineSegment StartX=-21.9 StartY=8.025 StartZ=0 EndX=21.9 EndY=8.025 EndZ=0
    g1: LineSegment StartX=21.9 StartY=8.025 StartZ=0 EndX=21.9 EndY=-8.025 EndZ=0
    g2: LineSegment StartX=21.9 StartY=-8.025 StartZ=0 EndX=-21.9 EndY=-8.025 EndZ=0
    g3: LineSegment StartX=-21.9 StartY=-8.025 StartZ=0 EndX=-21.9 EndY=8.025 EndZ=0
    g4: LineSegment StartX=-13.2344 StartY=5.33745 StartZ=0 EndX=12.5976 EndY=5.33745 EndZ=0
    g5: LineSegment StartX=12.5976 StartY=5.33745 StartZ=0 EndX=12.5976 EndY=-4.86779 EndZ=0
    g6: LineSegment StartX=12.5976 StartY=-4.86779 StartZ=0 EndX=-13.2344 EndY=-4.86779 EndZ=0
    g7: LineSegment StartX=-13.2344 StartY=-4.86779 StartZ=0 EndX=-13.2344 EndY=5.33745 EndZ=0
  constraints (18):
    c: Coincident(g0,g1)
    c: Coincident(g1,g2)
    c: Coincident(g2,g3)
    c: Coincident(g3,g0)
    c: Horizontal(g0)
    c: Horizontal(g2)
    c: Vertical(g1)
    c: Vertical(g3)
    c: Coincident(g1,g-4)
    c: Coincident(g0,g-3)
    c: Coincident(g4,g5)
    c: Coincident(g5,g6)
    c: Coincident(g6,g7)
    c: Coincident(g7,g4)
    c: Horizontal(g4)
    c: Horizontal(g6)
    c: Vertical(g5)
    c: Vertical(g7)
FEATURE [PartDesign::Pad] Pad005
  BaseFeature = -> Pad004
  Direction = (0,0,1)
  Length = 1
  Length2 = 10
  Profile = -> Sketch011
  ReferenceAxis = -> Sketch011 [N_Axis]
  Reversed = true
  Suppressed = false
  Type = 0
FEATURE [PartDesign::Fillet] Fillet
  Base = -> Pad005 [Edge5,Edge8,Edge1,Edge2]
  BaseFeature = -> Pad005
  Radius = 2
  SupportTransform = false
  Suppressed = false
  UseAllEdges = false
FEATURE [Sketcher::SketchObject] Sketch012
  ArcFitTolerance = 0
  AttachmentSupport = -> [XZ_Plane007]
  FullyConstrained = false
  MakeInternals = false
  MapMode = 5
  Placement = pos=(0,0,0) rot=(1,0,0;1.5708rad)
  sketch-geometry (4):
    g0: LineSegment StartX=-15.2868 StartY=5.66602 StartZ=0 EndX=-8.78676 EndY=5.66602 EndZ=0
    g1: LineSegment StartX=-8.78676 StartY=5.66602 StartZ=0 EndX=-8.78676 EndY=10.381 EndZ=0
    g2: LineSegment StartX=-8.78676 StartY=10.381 StartZ=0 EndX=-15.2868 EndY=10.381 EndZ=0
    g3: LineSegment StartX=-15.2868 StartY=10.381 StartZ=0 EndX=-15.2868 EndY=5.66602 EndZ=0
  constraints (9):
    c: Coincident(g0,g1)
    c: Coincident(g1,g2)
    c: Coincident(g2,g3)
    c: Coincident(g3,g0)
    c: Horizontal(g0)
    c: Horizontal(g2)
    c: Vertical(g1)
    c: Vertical(g3)
    c: DistanceX(g2,g2) = 6.5
FEATURE [PartDesign::Pocket] Pocket004
  BaseFeature = -> Fillet
  Direction = (0,1,-2e-16)
  Length = 5
  Length2 = 5
  Profile = -> Sketch012
  ReferenceAxis = -> Sketch012 [N_Axis]
  Suppressed = false
  Type = 1
FEATURE [Sketcher::SketchObject] Sketch014
  ArcFitTolerance = 0
  AttachmentSupport = -> [DatumPlane]
  FullyConstrained = true
  MakeInternals = false
  MapMode = 5
  sketch-geometry (12):
    g0: LineSegment StartX=2.25 StartY=6 StartZ=0 EndX=5.25 EndY=6 EndZ=0
    g1: LineSegment StartX=5.25 StartY=6 StartZ=0 EndX=5.25 EndY=-5.8 EndZ=0
    g2: LineSegment StartX=5.25 StartY=-5.8 StartZ=0 EndX=2.25 EndY=-5.8 EndZ=0
    g3: LineSegment StartX=2.25 StartY=-5.8 StartZ=0 EndX=2.25 EndY=6 EndZ=0
    g4: LineSegment StartX=-4.75 StartY=4.25 StartZ=0 EndX=-1.75 EndY=4.25 EndZ=0
    g5: LineSegment StartX=-1.75 StartY=4.25 StartZ=0 EndX=-1.75 EndY=-4.25 EndZ=0
    g6: LineSegment StartX=-1.75 StartY=-4.25 StartZ=0 EndX=-4.75 EndY=-4.25 EndZ=0
    g7: LineSegment StartX=-4.75 StartY=-4.25 StartZ=0 EndX=-4.75 EndY=4.25 EndZ=0
    g8: LineSegment StartX=-12.25 StartY=3.5 StartZ=0 EndX=-7.75 EndY=3.5 EndZ=0
    g9: LineSegment StartX=-7.75 StartY=3.5 StartZ=0 EndX=-7.75 EndY=-1 EndZ=0
    g10: LineSegment StartX=-7.75 StartY=-1 StartZ=0 EndX=-12.25 EndY=-1 EndZ=0
    g11: LineSegment StartX=-12.25 StartY=-1 StartZ=0 EndX=-12.25 EndY=3.5 EndZ=0
  constraints (35):
    c: Coincident(g0,g1)
    c: Coincident(g1,g2)
    c: Coincident(g2,g3)
    c: Coincident(g3,g0)
    c: Horizontal(g0)
    c: Horizontal(g2)
    c: Vertical(g1)
    c: Vertical(g3)
    c: Coincident(g4,g5)
    c: Coincident(g5,g6)
    c: Coincident(g6,g7)
    c: Coincident(g7,g4)
    c: Horizontal(g4)
    c: Horizontal(g6)
    c: Vertical(g5)
    c: Coincident(g8,g9)
    c: Coincident(g9,g10)
    c: Coincident(g10,g11)
    c: Coincident(g11,g8)
    c: Horizontal(g8)
    c: Horizontal(g10)
    c: Vertical(g9)
    c: Vertical(g11)
    c: DistanceY(g3,g3) = 11.8
    c: DistanceY(g5,g5) = 8.5
    c: DistanceY(g9,g9) = 4.5
    c: Equal(g8,g9)
    c: Equal(g4,g0)
    c: DistanceX(g2,g2) = 3
    c: DistanceY(g0) = 6
    c: Symmetric(g4,g6,g-1)
    c: DistanceX(g4,g-1) = 1.75
    c: DistanceX(g0) = 2.25
    c: DistanceX(g8,g4) = 3
    c: DistanceY(g8) = 3.5
FEATURE [Sketcher::SketchObject] Sketch015
  ArcFitTolerance = 0
  AttachmentSupport = -> [XY_Plane001]
  FullyConstrained = true
  MakeInternals = false
  MapMode = 5
  sketch-geometry (12):
    g0: LineSegment StartX=12 StartY=10 StartZ=0 EndX=13.5 EndY=10 EndZ=0
    g1: LineSegment StartX=13.5 StartY=10 StartZ=0 EndX=13.5 EndY=3 EndZ=0
    g2: LineSegment StartX=13.5 StartY=3 StartZ=0 EndX=16.5 EndY=3 EndZ=0
    g3: LineSegment StartX=16.5 StartY=3 StartZ=0 EndX=16.5 EndY=10 EndZ=0
    g4: LineSegment StartX=16.5 StartY=10 StartZ=0 EndX=18 EndY=10 EndZ=0
    g5: LineSegment StartX=18 StartY=10 StartZ=0 EndX=18 EndY=-10 EndZ=0
    g6: LineSegment StartX=18 StartY=-10 StartZ=0 EndX=16.5 EndY=-10 EndZ=0
    g7: LineSegment StartX=16.5 StartY=-10 StartZ=0 EndX=16.5 EndY=-3 EndZ=0
    g8: LineSegment StartX=16.5 StartY=-3 StartZ=0 EndX=13.5 EndY=-3 EndZ=0
    g9: LineSegment StartX=13.5 StartY=-3 StartZ=0 EndX=13.5 EndY=-10 EndZ=0
    g10: LineSegment StartX=13.5 StartY=-10 StartZ=0 EndX=12 EndY=-10 EndZ=0
    g11: LineSegment StartX=12 StartY=-10 StartZ=0 EndX=12 EndY=10 EndZ=0
  constraints (34):
    c: Coincident(g0,g1)
    c: Coincident(g1,g2)
    c: Coincident(g2,g3)
    c: Coincident(g3,g4)
    c: Coincident(g4,g5)
    c: Coincident(g5,g6)
    c: Horizontal(g6)
    c: Coincident(g6,g7)
    c: Vertical(g7)
    c: Coincident(g7,g8)
    c: Horizontal(g8)
    c: Coincident(g8,g9)
    c: Vertical(g9)
    c: Coincident(g9,g10)
    c: Horizontal(g10)
    c: Coincident(g10,g11)
    c: Coincident(g11,g0)
    c: Vertical(g11)
    c: DistanceX(g10,g5) = 6
    c: DistanceY(g8,g1) = 6
    c: Horizontal(g2)
    c: Horizontal(g4)
    c: Horizontal(g0)
    c: Vertical(g3)
    c: Vertical(g1)
    c: Equal(g4,g0)
    c: Equal(g10,g6)
    c: Equal(g5,g11)
    c: DistanceX(g4,g4) = 1.5
    c: DistanceY(g3,g3) = 7
    c: Symmetric(g1,g8,g-1)
    c: DistanceX(g0) = 12
    c: Symmetric(g5,g4,g-1)
    c: Equal(g7,g9)
FEATURE [PartDesign::Pocket] Pocket006
  BaseFeature = -> Pocket
  Direction = (0,0,-1)
  Length = 4.5
  Length2 = 5
  Profile = -> Sketch015
  ReferenceAxis = -> Sketch015 [N_Axis]
  Reversed = true
  Suppressed = false
  Type = 0
FEATURE [Sketcher::SketchObject] Sketch016
  ArcFitTolerance = 0
  AttachmentSupport = -> [XY_Plane001]
  FullyConstrained = false
  MakeInternals = false
  MapMode = 5
  sketch-geometry (8):
    g0: LineSegment StartX=16.5017 StartY=5.51624 StartZ=0 EndX=18.0017 EndY=5.51624 EndZ=0
    g1: LineSegment StartX=18.0017 StartY=5.51624 StartZ=0 EndX=18.0017 EndY=4.01624 EndZ=0
    g2: LineSegment StartX=18.0017 StartY=4.01624 StartZ=0 EndX=16.5017 EndY=4.01624 EndZ=0
    g3: LineSegment StartX=16.5017 StartY=4.01624 StartZ=0 EndX=16.5017 EndY=5.51624 EndZ=0
    g4: LineSegment StartX=16.5017 StartY=-4.01624 StartZ=0 EndX=18.0017 EndY=-4.01624 EndZ=0
    g5: LineSegment StartX=18.0017 StartY=-4.01624 StartZ=0 EndX=18.0017 EndY=-6.25804 EndZ=0
    g6: LineSegment StartX=18.0017 StartY=-6.25804 StartZ=0 EndX=16.5017 EndY=-6.25804 EndZ=0
    g7: LineSegment StartX=16.5017 StartY=-6.25804 StartZ=0 EndX=16.5017 EndY=-4.01624 EndZ=0
  constraints (20):
    c: Coincident(g0,g1)
    c: Coincident(g1,g2)
    c: Coincident(g2,g3)
    c: Coincident(g3,g0)
    c: Horizontal(g0)
    c: Horizontal(g2)
    c: Vertical(g1)
    c: Vertical(g3)
    c: Coincident(g4,g5)
    c: Coincident(g5,g6)
    c: Coincident(g6,g7)
    c: Coincident(g7,g4)
    c: Horizontal(g4)
    c: Horizontal(g6)
    c: Vertical(g5)
    c: Vertical(g7)
    c: Symmetric(g4,g1,g-1)
    c: Equal(g0,g6)
    c: Equal(g2,g3)
    c: DistanceX(g0,g0) = 1.5
FEATURE [PartDesign::Pocket] Pocket007
  BaseFeature = -> Pocket006
  Direction = (0,0,-1)
  Length = 5
  Length2 = 5
  Profile = -> Sketch016
  ReferenceAxis = -> Sketch016 [N_Axis]
  Reversed = true
  Suppressed = false
  Type = 1
FEATURE [PartDesign::Body] b_nano_spacer
  AllowCompound = false
  Group = -> [LCS_0,Sketch,Pad,Sketch001,Pocket,Sketch015,Pocket006,Sketch016,Pocket007]
  Origin = -> Origin001
  Tip = -> Pocket007
FEATURE [PartDesign::CoordinateSystem] LCS_0007
  AttacherType = Attacher::AttachEngine3D
  AttachmentSupport = -> [X_Axis008]
  MapMode = 2
FEATURE [Sketcher::SketchObject] Sketch017
  ArcFitTolerance = 0
  AttachmentSupport = -> [XZ_Plane008]
  FullyConstrained = true
  MakeInternals = false
  MapMode = 5
  Placement = pos=(0,0,0) rot=(1,0,0;1.5708rad)
  sketch-geometry (8):
    g0: LineSegment StartX=2.2 StartY=-21.5 StartZ=0 EndX=2.2 EndY=-4.5 EndZ=0
    g1: LineSegment StartX=2.2 StartY=-4.5 StartZ=0 EndX=0 EndY=-4.5 EndZ=0
    g2: LineSegment StartX=0 StartY=-4.5 StartZ=0 EndX=0 EndY=2.5 EndZ=0
    g3: LineSegment StartX=0 StartY=2.5 StartZ=0 EndX=6 EndY=2.5 EndZ=0
    g4: LineSegment StartX=6 StartY=2.5 StartZ=0 EndX=6 EndY=-6 EndZ=0
    g5: LineSegment StartX=6 StartY=-6 StartZ=0 EndX=4 EndY=-9 EndZ=0
    g6: LineSegment StartX=4 StartY=-9 StartZ=0 EndX=4 EndY=-21.5 EndZ=0
    g7: LineSegment StartX=4 StartY=-21.5 StartZ=0 EndX=2.2 EndY=-21.5 EndZ=0
  constraints (24):
    c: Vertical(g0)
    c: Horizontal(g1)
    c: Coincident(g1,g2)
    c: PointOnObject(g2,g-2)
    c: Vertical(g2)
    c: Horizontal(g3)
    c: Coincident(g3,g4)
    c: Vertical(g4)
    c: Coincident(g4,g5)
    c: Coincident(g5,g6)
    c: Vertical(g6)
    c: Coincident(g6,g7)
    c: Coincident(g7,g0)
    c: Horizontal(g7)
    c: DistanceX(g1,g1) = 2.2
    c: DistanceX(g4) = 6
    c: DistanceX(g6) = 4
    c: Coincident(g0,g1)
    c: Coincident(g2,g3)
    c: DistanceY(g2) = 2.5
    c: DistanceY(g6) = -21.5
    c: DistanceY(g4) = -6
    c: DistanceY(g5,g4) = 3
    c: DistanceY(g2,g2) = 7
FEATURE [PartDesign::Revolution] Revolution
  Angle = 360
  Angle2 = 60
  Axis = (0,2e-16,1)
  Base = (0,0,0)
  Placement = pos=(0,0,0) rot=(1,0,0;1.5708rad)
  Profile = -> Sketch017
  ReferenceAxis = -> Sketch017 [V_Axis]
  Reversed = true
  Suppressed = false
  Type = 0
FEATURE [Sketcher::SketchObject] Sketch018
  ArcFitTolerance = 0
  AttachmentSupport = -> [XY_Plane008]
  FullyConstrained = true
  MakeInternals = false
  MapMode = 5
  sketch-geometry (6):
    g0: LineSegment StartX=0 StartY=7 StartZ=0 EndX=2 EndY=7 EndZ=0
    g1: LineSegment StartX=2 StartY=7 StartZ=0 EndX=2 EndY=2 EndZ=0
    g2: LineSegment StartX=2 StartY=2 StartZ=0 EndX=7 EndY=2 EndZ=0
    g3: LineSegment StartX=7 StartY=2 StartZ=0 EndX=7 EndY=0 EndZ=0
    g4: LineSegment StartX=7 StartY=0 StartZ=0 EndX=0 EndY=0 EndZ=0
    g5: LineSegment StartX=0 StartY=0 StartZ=0 EndX=0 EndY=7 EndZ=0
  constraints (18):
    c: PointOnObject(g0,g-2)
    c: Coincident(g0,g1)
    c: Vertical(g1)
    c: Coincident(g1,g2)
    c: Horizontal(g2)
    c: Coincident(g2,g3)
    c: PointOnObject(g3,g-1)
    c: Vertical(g3)
    c: Coincident(g3,g4)
    c: Horizontal(g4)
    c: Coincident(g4,g5)
    c: Coincident(g5,g0)
    c: Vertical(g5)
    c: Equal(g0,g3)
    c: Horizontal(g0)
    c: DistanceY(g3,g3) = 2
    c: Equal(g2,g1)
    c: DistanceY(g1,g1) = 5
FEATURE [Sketcher::SketchObject] Sketch019
  ArcFitTolerance = 0
  AttachmentOffset = pos=(0,0,4) rot=(0,0,1;0rad)
  AttachmentSupport = -> [XY_Plane008]
  FullyConstrained = true
  MakeInternals = false
  MapMode = 5
  Placement = pos=(0,0,4) rot=(0,0,1;0rad)
  sketch-geometry (6):
    g0: LineSegment StartX=0 StartY=7.2 StartZ=0 EndX=2.2 EndY=7.2 EndZ=0
    g1: LineSegment StartX=2.2 StartY=7.2 StartZ=0 EndX=2.2 EndY=2.2 EndZ=0
    g2: LineSegment StartX=2.2 StartY=2.2 StartZ=0 EndX=7.2 EndY=2.2 EndZ=0
    g3: LineSegment StartX=7.2 StartY=2.2 StartZ=0 EndX=7.2 EndY=0 EndZ=0
    g4: LineSegment StartX=7.2 StartY=0 StartZ=0 EndX=0 EndY=0 EndZ=0
    g5: LineSegment StartX=0 StartY=0 StartZ=0 EndX=0 EndY=7.2 EndZ=0
  constraints (17):
    c: PointOnObject(g0,g-2)
    c: Horizontal(g0)
    c: Coincident(g0,g1)
    c: Vertical(g1)
    c: Coincident(g1,g2)
    c: Horizontal(g2)
    c: Coincident(g2,g3)
    c: PointOnObject(g3,g-1)
    c: Vertical(g3)
    c: Coincident(g3,g4)
    c: Coincident(g4,g-1)
    c: Coincident(g4,g5)
    c: Coincident(g5,g0)
    c: Equal(g3,g0)
    c: DistanceX(g0,g0) = 2.2
    c: Equal(g1,g2)
    c: DistanceY(g1,g1) = 5
FEATURE [PartDesign::SubtractiveLoft] SubtractiveLoft
  BaseFeature = -> Revolution
  Closed = false
  Placement = pos=(0,0,0) rot=(1,0,0;1.5708rad)
  Profile = -> Sketch018
  Ruled = false
  Sections = -> [Sketch019]
  Suppressed = false
FEATURE [PartDesign::PolarPattern] PolarPattern
  Angle = 360
  Axis = -> Sketch018 [N_Axis]
  BaseFeature = -> SubtractiveLoft
  Mode = 0
  Occurrences = 4
  Offset = 120
  Originals = -> [SubtractiveLoft]
  Placement = pos=(0,0,0) rot=(1,0,0;1.5708rad)
  Suppressed = false
  TransformMode = 0
FEATURE [Sketcher::SketchObject] Sketch020
  ArcFitTolerance = 0
  AttachmentOffset = pos=(0,0,-3.1) rot=(0,0,1;0rad)
  AttachmentSupport = -> [XY_Plane008]
  FullyConstrained = true
  MakeInternals = false
  MapMode = 5
  Placement = pos=(0,0,-3.1) rot=(0,0,1;0rad)
  sketch-geometry (8):
    g0: LineSegment StartX=-4.5 StartY=-7 StartZ=0 EndX=-4.5 EndY=9e-16 EndZ=0
    g1: ArcOfCircle CenterX=0 CenterY=0 CenterZ=0 NormalX=0 NormalY=0 NormalZ=1 AngleXU=0 Radius=4.5 StartAngle=1e-16 EndAngle=3.14159
    g2: LineSegment StartX=4.5 StartY=5e-16 StartZ=0 EndX=4.5 EndY=-7 EndZ=0
    g3: ArcOfCircle CenterX=0 CenterY=0 CenterZ=0 NormalX=0 NormalY=0 NormalZ=1 AngleXU=0 Radius=5.5 StartAngle=4.02261 EndAngle=5.40216
    g4: LineSegment StartX=-3.5 StartY=-4.24264 StartZ=0 EndX=-3.5 EndY=-7 EndZ=0
    g5: LineSegment StartX=-3.5 StartY=-7 StartZ=0 EndX=-4.5 EndY=-7 EndZ=0
    g6: LineSegment StartX=3.5 StartY=-4.24264 StartZ=0 EndX=3.5 EndY=-7 EndZ=0
    g7: LineSegment StartX=3.5 StartY=-7 StartZ=0 EndX=4.5 EndY=-7 EndZ=0
  constraints (22):
    c: Vertical(g0)
    c: Tangent(g0,g1) = 1.5708
    c: Tangent(g1,g2) = 1.5708
    c: Vertical(g2)
    c: Radius(g1) = 4.5
    c: Coincident(g3,g1)
    c: Coincident(g4,g5)
    c: Horizontal(g5)
    c: Vertical(g4)
    c: Coincident(g6,g7)
    c: Horizontal(g7)
    c: Vertical(g6)
    c: Equal(g5,g7)
    c: DistanceX(g7,g7) = 1
    c: Coincident(g3,g4)
    c: Coincident(g3,g6)
    c: Radius(g3) = 5.5
    c: Coincident(g0,g5)
    c: Coincident(g2,g7)
    c: DistanceY(g2,g2) = 7
    c: Coincident(g1,g-1)
    c: Equal(g4,g6)
FEATURE [PartDesign::Pocket] Pocket008
  BaseFeature = -> PolarPattern
  Direction = (0,0,-1)
  Length = 2.5
  Length2 = 5
  Placement = pos=(0,0,0) rot=(1,0,0;1.5708rad)
  Profile = -> Sketch020
  ReferenceAxis = -> Sketch020 [N_Axis]
  Suppressed = false
  Type = 0
FEATURE [Sketcher::SketchObject] Sketch021
  ArcFitTolerance = 0
  AttachmentSupport = -> [X_Axis008]
  FullyConstrained = true
  MakeInternals = false
  MapMode = 2
  sketch-geometry (1):
    g0: Circle CenterX=0 CenterY=0 CenterZ=0 NormalX=0 NormalY=0 NormalZ=1 AngleXU=0 Radius=3.25
  constraints (2):
    c: Coincident(g0,g-1)
    c: Diameter(g0) = 6.5
FEATURE [PartDesign::Pocket] Pocket009
  BaseFeature = -> Pocket008
  Direction = (0,0,-1)
  Length = 2.5
  Length2 = 5
  Placement = pos=(0,0,0) rot=(1,0,0;1.5708rad)
  Profile = -> Sketch021
  ReferenceAxis = -> Sketch021 [N_Axis]
  Suppressed = false
  Type = 4
FEATURE [PartDesign::Fillet] Fillet001
  Base = -> Pocket009 [Edge51,Edge36]
  BaseFeature = -> Pocket009
  Placement = pos=(0,0,0) rot=(1,0,0;1.5708rad)
  Radius = 1
  SupportTransform = false
  Suppressed = false
  UseAllEdges = false
FEATURE [PartDesign::Body] b_wrist_stands_magnetic
  AllowCompound = false
  Group = -> [LCS_0007,Sketch017,Revolution,Sketch018,Sketch019,SubtractiveLoft,PolarPattern,Sketch020,Pocket008,Sketch021,Pocket009,Fillet001]
  Origin = -> Origin008
  Tip = -> Fillet001
FEATURE [PartDesign::CoordinateSystem] LCS_0008
  AttacherType = Attacher::AttachEngine3D
  AttachmentSupport = -> [X_Axis009]
  MapMode = 2
FEATURE [Sketcher::SketchObject] Sketch022
  ArcFitTolerance = 0
  AttachmentOffset = pos=(0,0,26) rot=(0,0,1;0rad)
  AttachmentSupport = -> [XZ_Plane009]
  FullyConstrained = true
  MakeInternals = false
  MapMode = 5
  Placement = pos=(0,-26,5.8e-15) rot=(1,0,0;1.5708rad)
  sketch-geometry (7):
    g0: LineSegment StartX=-24.5 StartY=0 StartZ=0 EndX=33.5 EndY=0 EndZ=0
    g1: LineSegment StartX=33.5 StartY=0 StartZ=0 EndX=39.5 EndY=-6.5 EndZ=0
    g2: LineSegment StartX=39.5 StartY=-6.5 StartZ=0 EndX=42.4392 EndY=-3.78688 EndZ=0
    g3: LineSegment StartX=-44.9526 StartY=-7.73015 StartZ=0 EndX=-41.5 EndY=-9.75 EndZ=0
    g4: ArcOfCircle CenterX=-24.5 CenterY=-19.6955 CenterZ=0 NormalX=0 NormalY=0 NormalZ=1 AngleXU=0 Radius=19.6955 StartAngle=1.5708 EndAngle=2.61225
    g5: ArcOfCircle CenterX=0.624932 CenterY=-47.4592 CenterZ=0 NormalX=0 NormalY=0 NormalZ=1 AngleXU=0 Radius=60.4624 StartAngle=0.80713 EndAngle=2.42465
    g6: GeomPoint [constr] X=0 Y=13 Z=0
  constraints (20):
    c: PointOnObject(g0,g-1)
    c: PointOnObject(g0,g-1)
    c: Coincident(g0,g1)
    c: Coincident(g1,g2)
    c: Perpendicular(g3,g4) = 4.71239
    c: DistanceX(g0) = -24.5
    c: Tangent(g4,g0) = 1.5708
    c: DistanceX(g0) = 33.5
    c: DistanceX(g0,g1) = 6
    c: DistanceY(g1,g0) = 6.5
    c: Perpendicular(g1,g2)
    c: Equal(g2,g3)
    c: DistanceY(g3) = -9.75
    c: DistanceX(g3) = -41.5
    c: Coincident(g5,g3)
    c: Coincident(g5,g2)
    c: Distance(g3) = 4
    c: PointOnObject(g6,g5)
    c: PointOnObject(g6,g-2)
    c: DistanceY(g6) = 13
FEATURE [Sketcher::SketchObject] Sketch023
  ArcFitTolerance = 0
  AttachmentSupport = -> [XZ_Plane009]
  FullyConstrained = true
  MakeInternals = false
  MapMode = 5
  Placement = pos=(0,0,0) rot=(1,0,0;1.5708rad)
  sketch-geometry (7):
    g0: LineSegment StartX=-24.5 StartY=0 StartZ=0 EndX=33.5 EndY=0 EndZ=0
    g1: LineSegment StartX=33.5 StartY=0 StartZ=0 EndX=39.5 EndY=-6.5 EndZ=0
    g2: LineSegment StartX=39.5 StartY=-6.5 StartZ=0 EndX=42.4392 EndY=-3.78688 EndZ=0
    g3: LineSegment StartX=-44.9526 StartY=-7.73015 StartZ=0 EndX=-41.5 EndY=-9.75 EndZ=0
    g4: ArcOfCircle CenterX=-24.5 CenterY=-19.6955 CenterZ=0 NormalX=0 NormalY=0 NormalZ=1 AngleXU=0 Radius=19.6955 StartAngle=1.5708 EndAngle=2.61225
    g5: ArcOfCircle CenterX=2.16236 CenterY=-81.5321 CenterZ=0 NormalX=0 NormalY=0 NormalZ=1 AngleXU=0 Radius=87.5588 StartAngle=1.0928 EndAngle=2.13897
    g6: GeomPoint [constr] X=0 Y=6 Z=0
  constraints (20):
    c: PointOnObject(g0,g-1)
    c: PointOnObject(g0,g-1)
    c: Coincident(g0,g1)
    c: Coincident(g1,g2)
    c: Perpendicular(g3,g4) = 4.71239
    c: DistanceX(g0) = -24.5
    c: Tangent(g4,g0) = 1.5708
    c: DistanceX(g0) = 33.5
    c: DistanceX(g0,g1) = 6
    c: DistanceY(g1,g0) = 6.5
    c: Perpendicular(g1,g2)
    c: Equal(g2,g3)
    c: DistanceY(g3) = -9.75
    c: DistanceX(g3) = -41.5
    c: Coincident(g5,g3)
    c: Coincident(g5,g2)
    c: Distance(g3) = 4
    c: PointOnObject(g6,g5)
    c: PointOnObject(g6,g-2)
    c: DistanceY(g6) = 6
FEATURE [PartDesign::AdditiveLoft] AdditiveLoft001
  Closed = false
  Placement = pos=(0,0,0) rot=(1,0,0;1.5708rad)
  Profile = -> Sketch022
  Ruled = false
  Sections = -> [Sketch023]
  Suppressed = false
FEATURE [Sketcher::SketchObject] Sketch024
  ArcFitTolerance = 0
  AttachmentSupport = -> [XY_Plane009]
  FullyConstrained = false
  MakeInternals = false
  MapMode = 5
  sketch-geometry (11):
    g0: LineSegment StartX=-22 StartY=8.4e-15 StartZ=0 EndX=9.99091 EndY=-0.825847 EndZ=0
    g1: LineSegment StartX=9.99091 StartY=-0.825847 StartZ=0 EndX=33.0058 EndY=-3.41654 EndZ=0
    g2: LineSegment StartX=33.0058 StartY=-3.41654 StartZ=0 EndX=43.1901 EndY=-13.2747 EndZ=0
    g3: LineSegment StartX=43.1901 StartY=-13.2747 StartZ=0 EndX=43.1901 EndY=17.2246 EndZ=0
    g4: LineSegment StartX=43.1901 StartY=17.2246 StartZ=0 EndX=-48.8443 EndY=17.2246 EndZ=0
    g5: LineSegment StartX=-48.8443 StartY=17.2246 StartZ=0 EndX=-48.8443 EndY=-33.3988 EndZ=0
    g6: LineSegment StartX=-48.8443 StartY=-33.3988 StartZ=0 EndX=-45 EndY=-33.3988 EndZ=0
    g7: LineSegment StartX=-45 StartY=-33.3988 StartZ=0 EndX=-45 EndY=-26 EndZ=0
    g8: ArcOfParabola CenterX=-34.081 CenterY=-3 CenterZ=0 NormalX=0 NormalY=0 NormalZ=1 Focal=8.67924 AngleXU=-1.00009 StartAngle=-21.6138 EndAngle=11.787
    g9: GeomPoint [constr] X=-29.3922 Y=-10.3037 Z=0
    g10: LineSegment [constr] StartX=-34.081 StartY=-3 StartZ=0 EndX=-29.3922 EndY=-10.3037 EndZ=0
  constraints (21):
    c: PointOnObject(g0,g-1)
    c: Coincident(g0,g1)
    c: Coincident(g1,g2)
    c: Coincident(g2,g3)
    c: Vertical(g3)
    c: Coincident(g3,g4)
    c: Horizontal(g4)
    c: Coincident(g4,g5)
    c: Vertical(g5)
    c: Coincident(g5,g6)
    c: Horizontal(g6)
    c: Coincident(g6,g7)
    c: Vertical(g7)
    c: InternalAlignment(g9,g8)
    c: InternalAlignment(g10,g8)
    c: Coincident(g7,g8)
    c: DistanceX(g6) = -45
    c: DistanceY(g7) = -26
    c: DistanceX(g0) = -22
    c: Tangent(g8,g0) = -1.5708
    c: DistanceY(g8,g0) = 3
FEATURE [PartDesign::Pocket] Pocket010
  BaseFeature = -> AdditiveLoft001
  Direction = (0,0,-1)
  Length = 21
  Length2 = 5
  Midplane = true
  Placement = pos=(0,0,0) rot=(1,0,0;1.5708rad)
  Profile = -> Sketch024
  ReferenceAxis = -> Sketch024 [N_Axis]
  Suppressed = false
  Type = 0
FEATURE [Sketcher::SketchObject] Sketch025
  ArcFitTolerance = 0
  AttachmentOffset = pos=(0,0,17) rot=(0,0,1;0rad)
  AttachmentSupport = -> [XY_Plane009]
  FullyConstrained = true
  MakeInternals = false
  MapMode = 5
  Placement = pos=(0,0,17) rot=(0,0,1;0rad)
  sketch-geometry (1):
    g0: Circle CenterX=0 CenterY=-21 CenterZ=0 NormalX=0 NormalY=0 NormalZ=1 AngleXU=0 Radius=2.75
  constraints (3):
    c: PointOnObject(g0,g-2)
    c: Diameter(g0) = 5.5
    c: DistanceY(g0) = -21
FEATURE [PartDesign::Hole] Hole
  BaseFeature = -> Pocket010
  CustomThreadClearance = 0
  Depth = 25
  DepthType = 0
  Diameter = 3.9
  DrillForDepth = false
  DrillPoint = 1
  DrillPointAngle = 118
  HoleCutCountersinkAngle = 90
  HoleCutCustomValues = false
  HoleCutDepth = 14
  HoleCutDiameter = 6.7
  HoleCutType = 1
  ModelThread = false
  Placement = pos=(0,0,0) rot=(1,0,0;1.5708rad)
  Profile = -> Sketch025
  Suppressed = false
  Tapered = false
  TaperedAngle = 90
  ThreadClass = 0
  ThreadDepth = 25
  ThreadDepthType = 0
  ThreadDirection = 0
  ThreadFit = 0
  ThreadSize = 10
  ThreadType = 1
  Threaded = false
  UseCustomThreadClearance = false
FEATURE [PartDesign::Body] b_led_strip_base
  AllowCompound = false
  Group = -> [LCS_0008,Sketch022,Sketch023,AdditiveLoft001,Sketch024,Pocket010,Sketch025,Hole]
  Origin = -> Origin009
  Tip = -> Hole
FEATURE [PartDesign::Plane] DatumPlane001
  AttachmentOffset = pos=(0,0,9) rot=(1,0,0;0.523599rad)
  AttachmentSupport = -> [DatumPlane]
  Length = 61.6877
  MapMode = 5
  Placement = pos=(0,0,9) rot=(1,0,0;0.523599rad)
  ResizeMode = 0
  Width = 79.989
FEATURE [PartDesign::CoordinateSystem] LCS_0005
  AttacherType = Attacher::AttachEngine3D
  AttachmentOffset = pos=(-12,-1,0) rot=(0,0,1;0rad)
  AttachmentSupport = -> [DatumPlane001]
  MapMode = 2
  Placement = pos=(-12,-0.866025,8.5) rot=(1,0,0;0.523599rad)
FEATURE [Sketcher::SketchObject] Sketch006
  ArcFitTolerance = 0
  AttachmentOffset = pos=(-12,0,0) rot=(0,0,1;0rad)
  AttachmentSupport = -> [DatumPlane001]
  FullyConstrained = true
  MakeInternals = false
  MapMode = 5
  Placement = pos=(-12,0,9) rot=(1,0,0;0.523599rad)
  sketch-geometry (4):
    g0: LineSegment StartX=-3 StartY=4 StartZ=0 EndX=3 EndY=4 EndZ=0
    g1: LineSegment StartX=3 StartY=4 StartZ=0 EndX=3 EndY=-4 EndZ=0
    g2: LineSegment StartX=3 StartY=-4 StartZ=0 EndX=-3 EndY=-4 EndZ=0
    g3: LineSegment StartX=-3 StartY=-4 StartZ=0 EndX=-3 EndY=4 EndZ=0
  constraints (10):
    c: Coincident(g0,g1)
    c: Coincident(g1,g2)
    c: Coincident(g2,g3)
    c: Coincident(g3,g0)
    c: Horizontal(g2)
    c: Vertical(g1)
    c: DistanceX(g2,g2) = 6
    c: Symmetric(g0,g0,g-2)
    c: DistanceY(g1,g1) = 8
    c: Symmetric(g0,g2,g-1)
FEATURE [PartDesign::AdditiveLoft] AdditiveLoft
  BaseFeature = -> Pad003
  Closed = false
  Profile = -> Sketch006
  Ruled = true
  Sections = -> [Sketch008]
  Suppressed = false
FEATURE [Sketcher::SketchObject] Sketch009
  ArcFitTolerance = 0
  AttachmentSupport = -> [LCS_0005]
  FullyConstrained = true
  MakeInternals = false
  MapMode = 5
  Placement = pos=(-12,-0.866025,8.5) rot=(1,0,0;0.523599rad)
  sketch-geometry (1):
    g0: Circle CenterX=0 CenterY=0 CenterZ=0 NormalX=0 NormalY=0 NormalZ=1 AngleXU=0 Radius=1.5
  constraints (2):
    c: Coincident(g0,g-1)
    c: Diameter(g0) = 3
FEATURE [PartDesign::Pocket] Pocket003
  BaseFeature = -> AdditiveLoft
  Direction = (0,0.5,-0.866025)
  Length = 6
  Length2 = 5
  Profile = -> Sketch009
  ReferenceAxis = -> Sketch009 [N_Axis]
  Suppressed = false
  Type = 0
FEATURE [PartDesign::Pocket] Pocket005
  BaseFeature = -> Pocket003
  Direction = (0,0,-1)
  Length = 1.5
  Length2 = 5
  Profile = -> Sketch014
  ReferenceAxis = -> Sketch014 [N_Axis]
  Suppressed = false
  Type = 0
FEATURE [PartDesign::Chamfer] Chamfer001
  Angle = 32
  Base = -> Pocket005 [Edge70]
  BaseFeature = -> Pocket005
  ChamferType = 2
  FlipDirection = false
  Size = 1
  Size2 = 1
  SupportTransform = false
  Suppressed = false
  UseAllEdges = false
FEATURE [PartDesign::Chamfer] Chamfer002
  Angle = 30
  Base = -> Chamfer001 [Edge15]
  BaseFeature = -> Chamfer001
  ChamferType = 2
  FlipDirection = false
  Size = 1
  Size2 = 1
  SupportTransform = false
  Suppressed = false
  UseAllEdges = false
FEATURE [Sketcher::SketchObject] Sketch026
  ArcFitTolerance = 0
  AttachmentOffset = pos=(0,0,10) rot=(0,0,1;0rad)
  AttachmentSupport = -> [YZ_Plane006]
  FullyConstrained = false
  MakeInternals = false
  MapMode = 5
  Placement = pos=(10,0,0) rot=(0.57735,0.57735,0.57735;2.0944rad)
  sketch-geometry (2):
    g0: Circle CenterX=-6.5755 CenterY=0 CenterZ=0 NormalX=0 NormalY=0 NormalZ=1 AngleXU=0 Radius=0.7
    g1: Circle CenterX=6.5755 CenterY=0 CenterZ=0 NormalX=0 NormalY=0 NormalZ=1 AngleXU=0 Radius=0.7
  constraints (4):
    c: PointOnObject(g0,g-1)
    c: Diameter(g0) = 1.4
    c: Equal(g1,g0)
    c: Symmetric(g1,g0,g-2)
FEATURE [PartDesign::Pocket] Pocket011
  BaseFeature = -> Chamfer002
  Direction = (-1,0,0)
  Length = 5
  Length2 = 5
  Midplane = true
  Profile = -> Sketch026
  ReferenceAxis = -> Sketch026 [N_Axis]
  Suppressed = false
  Type = 0
FEATURE [PartDesign::Mirrored] Mirrored
  BaseFeature = -> Pocket011
  MirrorPlane = -> YZ_Plane006
  Originals = -> [Pocket011]
  Suppressed = false
  TransformMode = 0
FEATURE [PartDesign::Body] b_oled_case_bottom
  AllowCompound = false
  Group = -> [LCS_0005,Sketch006,LCS_2,DatumPlane,Sketch007,Pad003,Sketch008,AdditiveLoft,Sketch009,Pocket003,Sketch014,Pocket005,DatumPlane001,Chamfer001,Chamfer002,Sketch026,Pocket011,Mirrored]
  Origin = -> Origin006
  Tip = -> Mirrored
FEATURE [Sketcher::SketchObject] Sketch027
  ArcFitTolerance = 0
  AttachmentOffset = pos=(0,0,10) rot=(0,0,1;0rad)
  AttachmentSupport = -> [YZ_Plane007]
  FullyConstrained = true
  MakeInternals = false
  MapMode = 5
  Placement = pos=(10,0,0) rot=(0.57735,0.57735,0.57735;2.0944rad)
  sketch-geometry (2):
    g0: Circle CenterX=6.62 CenterY=4.4 CenterZ=0 NormalX=0 NormalY=0 NormalZ=1 AngleXU=0 Radius=0.5
    g1: Circle CenterX=-6.62 CenterY=4.4 CenterZ=0 NormalX=0 NormalY=0 NormalZ=1 AngleXU=0 Radius=0.5
  constraints (5):
    c: DistanceY(g0) = 4.4
    c: Diameter(g0) = 1
    c: DistanceX(g0) = 6.62
    c: Symmetric(g1,g0,g-2)
    c: Equal(g1,g0)
FEATURE [PartDesign::Pad] Pad006
  BaseFeature = -> Pocket004
  Direction = (1,0,0)
  Length = 4
  Length2 = 10
  Midplane = true
  Profile = -> Sketch027
  ReferenceAxis = -> Sketch027 [N_Axis]
  Suppressed = false
  Type = 0
FEATURE [PartDesign::Mirrored] Mirrored001
  BaseFeature = -> Pad006
  MirrorPlane = -> YZ_Plane007
  Originals = -> [Pad006]
  Suppressed = false
  TransformMode = 0
FEATURE [PartDesign::Body] b_oled_case_top
  AllowCompound = false
  Group = -> [LCS_0006,Sketch010,Pad004,Sketch011,Pad005,Fillet,Sketch012,Pocket004,Sketch027,Pad006,Mirrored001]
  Origin = -> Origin007
  Tip = -> Mirrored001
FEATURE [Part::FeaturePython] Screw  label="M3x10-Screw"  # WARN: FeaturePython — macro-defined, semantics opaque (R4)
  AssemblyType = Part::Link
  AttachedBy = Origin
  AttachedTo = m3_attach#LCS_1
  AttachmentOffset = pos=(0,0,5) rot=(0,0,1;0rad)
  Diameter = 4
  Invert = false
  LeftHanded = false
  Length = 3
  LengthCustom = 10
  MatchOuter = false
  OffsetAngle = 0
  Placement = pos=(3,6.5,5) rot=(0,0,1;1.5708rad)
  SolverId = Asm4EE
  Thread = false
  Type = 74
  expr: Placement = m3_attach.Placement * LCS_1.Placement * AttachmentOffset
FEATURE [App::Link] led_strip_base
  AssemblyType = Part::Link
  AttachedBy = #LCS_0008
  AttachedTo = Parent Assembly#LCS_Origin
  AttachmentOffset = pos=(54,0,-63) rot=(0,0,1;0rad)
  LinkPlacement = pos=(54,0,-63) rot=(0,0,1;0rad)
  LinkedObject = -> b_led_strip_base
  Placement = pos=(54,0,-63) rot=(0,0,1;0rad)
  SolverId = Asm4EE
  expr: Placement = LCS_Origin.Placement * AttachmentOffset * LCS_0008.Placement ^ -1
FEATURE [PartDesign::CoordinateSystem] LCS_Origin001
  AttacherType = Attacher::AttachEngine3D
  AttachmentSupport = -> [X_Axis010]
  MapMode = 2
FEATURE [Sketcher::SketchObject] Sketch028
  ArcFitTolerance = 1e-06
  AttachmentSupport = -> [XY_Plane010]
  FullyConstrained = true
  MakeInternals = false
  MapMode = 5
  sketch-geometry (9):
    g0: LineSegment StartX=-2 StartY=0 StartZ=0 EndX=-2 EndY=10 EndZ=0
    g1: LineSegment StartX=-2 StartY=10 StartZ=0 EndX=21 EndY=10 EndZ=0
    g2: LineSegment StartX=21 StartY=10 StartZ=0 EndX=21 EndY=7 EndZ=0
    g3: LineSegment StartX=21 StartY=7 StartZ=0 EndX=31 EndY=7 EndZ=0
    g4: LineSegment StartX=31 StartY=7 StartZ=0 EndX=31 EndY=4 EndZ=0
    g5: LineSegment StartX=31 StartY=4 StartZ=0 EndX=21 EndY=4 EndZ=0
    g6: LineSegment StartX=21 StartY=4 StartZ=0 EndX=21 EndY=0 EndZ=0
    g7: LineSegment StartX=21 StartY=0 StartZ=0 EndX=-2 EndY=0 EndZ=0
    g8: Circle CenterX=16.7 CenterY=5 CenterZ=0 NormalX=0 NormalY=0 NormalZ=1 AngleXU=0 Radius=2
  constraints (27):
    c: Coincident(g0,g1)
    c: Horizontal(g1)
    c: Coincident(g1,g2)
    c: Coincident(g2,g3)
    c: Horizontal(g3)
    c: Coincident(g3,g4)
    c: Coincident(g4,g5)
    c: Horizontal(g5)
    c: Coincident(g5,g6)
    c: PointOnObject(g6,g-1)
    c: Vertical(g6)
    c: Coincident(g6,g7)
    c: Vertical(g2)
    c: DistanceX(g1,g1) = 23
    c: DistanceX(g3,g3) = 10
    c: Vertical(g4)
    c: Vertical(g5,g2)
    c: DistanceY(g0,g0) = 10
    c: DistanceY(g4,g4) = 3
    c: DistanceY(g6,g6) = 4
    c: DistanceX(g8) = 16.7
    c: Diameter(g8) = 4
    c: DistanceY(g8) = 5
    c: Vertical(g0)
    c: Coincident(g0,g7)
    c: PointOnObject(g0,g-1)
    c: DistanceX(g0) = -2
FEATURE [PartDesign::Pad] Pad007
  Direction = (0,0,1)
  Length = 5
  Length2 = 10
  Profile = -> Sketch028
  ReferenceAxis = -> Sketch028 [N_Axis]
  Refine = true
  Suppressed = false
  Type = 0
FEATURE [Sketcher::SketchObject] Sketch029
  ArcFitTolerance = 1e-06
  AttachmentSupport = -> [XY_Plane010]
  FullyConstrained = true
  MakeInternals = false
  MapMode = 5
  sketch-geometry (8):
    g0: LineSegment StartX=-2 StartY=10.75 StartZ=0 EndX=-2 EndY=8.25 EndZ=0
    g1: LineSegment StartX=-2 StartY=8.25 StartZ=0 EndX=14 EndY=8.25 EndZ=0
    g2: LineSegment StartX=14 StartY=8.25 StartZ=0 EndX=14 EndY=10.75 EndZ=0
    g3: LineSegment StartX=14 StartY=10.75 StartZ=0 EndX=7.5 EndY=10.75 EndZ=0
    g4: LineSegment StartX=4.5 StartY=10.75 StartZ=0 EndX=4.5 EndY=12.75 EndZ=0
    g5: LineSegment StartX=4.5 StartY=12.75 StartZ=0 EndX=7.5 EndY=12.75 EndZ=0
    g6: LineSegment StartX=7.5 StartY=12.75 StartZ=0 EndX=7.5 EndY=10.75 EndZ=0
    g7: LineSegment StartX=4.5 StartY=10.75 StartZ=0 EndX=-2 EndY=10.75 EndZ=0
  constraints (24):
    c: Coincident(g0,g1)
    c: Coincident(g1,g2)
    c: Coincident(g2,g3)
    c: Coincident(g7,g0)
    c: Vertical(g0)
    c: Vertical(g2)
    c: Horizontal(g1)
    c: Horizontal(g3)
    c: DistanceY(g0,g0) = 2.5
    c: DistanceX(g0) = -2
    c: DistanceX(g1,g1) = 16
    c: Vertical(g4)
    c: Coincident(g4,g5)
    c: Horizontal(g5)
    c: Coincident(g5,g6)
    c: Vertical(g6)
    c: Coincident(g3,g6)
    c: Equal(g3,g7)
    c: DistanceX(g5,g5) = 3
    c: Horizontal(g7)
    c: Horizontal(g3,g4)
    c: Coincident(g4,g7)
    c: DistanceY(g4,g4) = 2
    c: DistanceY(g0) = 10.75
FEATURE [PartDesign::Pad] Pad008
  BaseFeature = -> Pad007
  Direction = (0,0,1)
  Length = 10
  Length2 = 10
  Profile = -> Sketch029
  ReferenceAxis = -> Sketch029 [N_Axis]
  Refine = true
  Suppressed = false
  Type = 0
FEATURE [PartDesign::Body] b_diode_press_template  label="b_diode_press_new"
  AllowCompound = false
  Group = -> [LCS_Origin001,Sketch028,Pad007,Sketch029,Pad008]
  Origin = -> Origin010
  Tip = -> Pad008
FEATURE [App::DocumentObjectGroup] Parts
  Group = -> [b_nano_spacer,b_m3_attach,p_thumb_spacer,p_oled,b_oled_case_bottom,b_oled_case_top,b_wrist_stands_magnetic,b_led_strip_base,b_diode_press_template]
FEATURE [App::Link] diode_press_new
  AttachedBy = #LCS_Origin001
  AttachedTo = Parent Assembly#LCS_Origin
  AttachmentOffset = pos=(41,-47.4,-112) rot=(0,1,0;4.18879rad)
  LinkPlacement = pos=(41,-47.4,-112) rot=(0,1,0;4.18879rad)
  LinkedObject = -> b_diode_press_template
  Placement = pos=(41,-47.4,-112) rot=(0,1,0;4.18879rad)
  SolverId = Asm4EE
  expr: Placement = LCS_Origin.Placement * AttachmentOffset * LCS_Origin001.Placement ^ -1
FEATURE [App::Part] Model  label="Assembly"
  AssemblyType = Part::Link
  Group = -> [LCS_Origin,Constraints,Variables,Configurations,thumb_spacer,m3_attach,oled,oled_case_bottom,oled_case_top,Screw,led_strip_base,diode_press_new]
  Origin = -> Origin
  Type = Assembly
